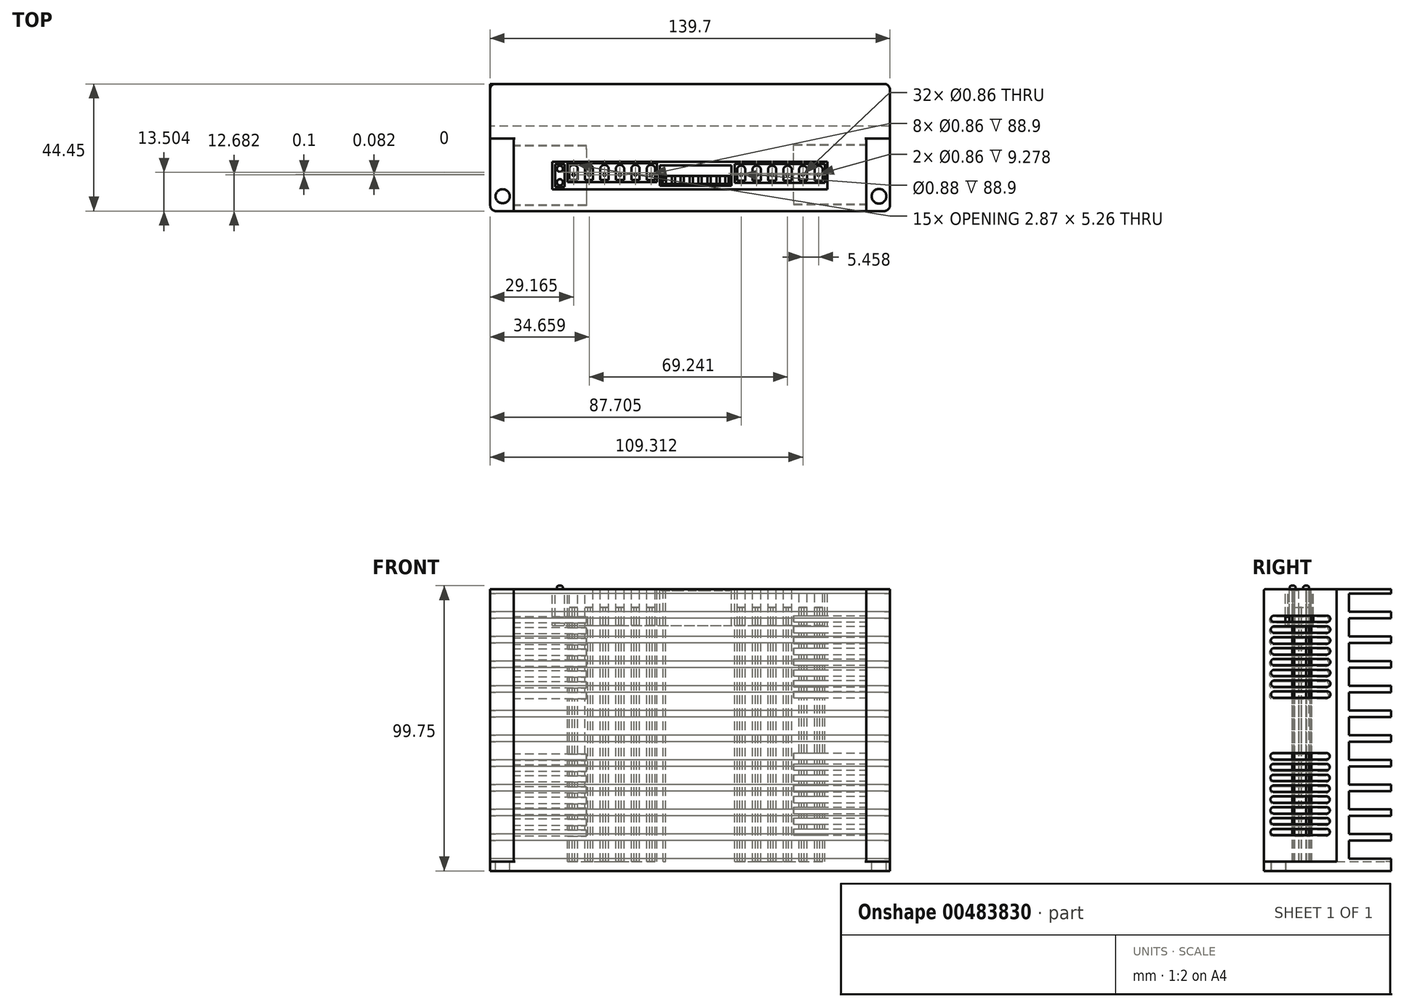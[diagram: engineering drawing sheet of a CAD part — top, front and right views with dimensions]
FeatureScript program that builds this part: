
annotation { "Feature Type Name" : "Feature", "Feature Type Description" : "" }
export const myFeature = defineFeature(function(context is Context, id is Id, definition is map)
    precondition{}
    {
        {
            var Q0;
            Q0=qCreatedBy(makeId("Top.planeOp"),FACE);
            var sketch = newSketch(context, id + "F0", { "sketchPlane" : qUnion([Q0])});
            skLineSegment(sketch, "E0.bottom", {"start": v(61.6, 12.7) * mm, "end": v(-61.6, 12.7) * mm});
            skLineSegment(sketch, "E0.top", {"start": v(61.6, -12.7) * mm, "end": v(-61.6, -12.7) * mm});
            skLineSegment(sketch, "E0.left", {"start": v(61.6, 12.7) * mm, "end": v(61.6, -12.7) * mm});
            skLineSegment(sketch, "E0.right", {"start": v(-61.6, 12.7) * mm, "end": v(-61.6, -12.7) * mm});
            skPoint(sketch, "E0.middle", {"position": v(0, 0) * mm});
            skLineSegment(sketch, "E1.bottom", {"start": v(69.85, 12.7) * mm, "end": v(-69.85, 12.7) * mm});
            skLineSegment(sketch, "E1.top", {"start": v(69.85, 31.75) * mm, "end": v(-69.85, 31.75) * mm});
            skLineSegment(sketch, "E1.left", {"start": v(69.85, 12.7) * mm, "end": v(69.85, 31.75) * mm});
            skLineSegment(sketch, "E1.right", {"start": v(-69.85, 12.7) * mm, "end": v(-69.85, 31.75) * mm});
            skPoint(sketch, "E1.middle", {"position": v(0, 22.23) * mm});
            skLineSegment(sketch, "E2.bottom", {"start": v(-48.06, -5.18) * mm, "end": v(48.06, -5.18) * mm});
            skLineSegment(sketch, "E2.top", {"start": v(-48.06, 4.6) * mm, "end": v(48.06, 4.6) * mm});
            skLineSegment(sketch, "E2.left", {"start": v(-48.06, 4.6) * mm, "end": v(-48.06, -5.18) * mm});
            skLineSegment(sketch, "E2.right", {"start": v(48.06, 4.6) * mm, "end": v(48.06, -5.18) * mm});
            skLineSegment(sketch, "E3.bottom", {"start": v(-47.05, 3.69) * mm, "end": v(-43.77, 3.69) * mm});
            skLineSegment(sketch, "E3.top", {"start": v(-47.05, -4.28) * mm, "end": v(-43.77, -4.28) * mm});
            skLineSegment(sketch, "E3.left", {"start": v(-47.05, 3.69) * mm, "end": v(-47.05, -4.28) * mm});
            skLineSegment(sketch, "E3.right", {"start": v(-43.77, 3.69) * mm, "end": v(-43.77, -4.28) * mm});
            skLineSegment(sketch, "E4.bottom", {"start": v(-42.75, 4.07) * mm, "end": v(-11.5, 4.07) * mm});
            skLineSegment(sketch, "E4.top", {"start": v(-42.75, -2.56) * mm, "end": v(-11.5, -2.56) * mm});
            skLineSegment(sketch, "E4.left", {"start": v(-42.75, 4.07) * mm, "end": v(-42.75, -2.56) * mm});
            skLineSegment(sketch, "E4.right", {"start": v(-11.5, 4.07) * mm, "end": v(-11.5, -2.56) * mm});
            skLineSegment(sketch, "E5.bottom", {"start": v(15.6, 3.79) * mm, "end": v(47.16, 3.79) * mm});
            skLineSegment(sketch, "E5.top", {"start": v(15.6, -2.8) * mm, "end": v(47.16, -2.8) * mm});
            skLineSegment(sketch, "E5.left", {"start": v(15.6, 3.79) * mm, "end": v(15.6, -2.8) * mm});
            skLineSegment(sketch, "E5.right", {"start": v(47.16, 3.79) * mm, "end": v(47.16, -2.8) * mm});
            skLineSegment(sketch, "E6.bottom", {"start": v(-10.49, 3.24) * mm, "end": v(14.52, 3.24) * mm});
            skLineSegment(sketch, "E6.top", {"start": v(-10.49, -3.8) * mm, "end": v(14.52, -3.8) * mm});
            skLineSegment(sketch, "E6.left", {"start": v(-10.49, 3.24) * mm, "end": v(-10.49, -3.8) * mm});
            skLineSegment(sketch, "E6.right", {"start": v(14.52, 3.24) * mm, "end": v(14.52, -3.8) * mm});
            skLineSegment(sketch, "E7", {"start": v(-42.12, -1.82) * mm, "end": v(-39.25, -1.82) * mm});
            skLineSegment(sketch, "E8", {"start": v(-42.12, -1.82) * mm, "end": v(-42.12, 2.37) * mm});
            skLineSegment(sketch, "E9", {"start": v(-39.25, -1.82) * mm, "end": v(-39.25, 2.37) * mm});
            skArc(sketch, "E10", {"start": v(-39.25, 2.37) * mm, "mid": v(-40.68, 3.43) * mm, "end": v(-42.12, 2.37) * mm});
            skCircle(sketch, "E11", {"center": v(-45.45, 2.08) * mm, "radius": 1.05 * mm});
            skCircle(sketch, "E12", {"center": v(-45.45, -2.65) * mm, "radius": 1.07 * mm});
            skLineSegment(sketch, "E13.1.0.0", {"start": v(-36.7, -1.83) * mm, "end": v(-36.7, 2.36) * mm});
            skLineSegment(sketch, "E13.1.0.1", {"start": v(-36.7, -1.83) * mm, "end": v(-33.84, -1.83) * mm});
            skLineSegment(sketch, "E13.1.0.2", {"start": v(-33.84, -1.83) * mm, "end": v(-33.84, 2.36) * mm});
            skArc(sketch, "E13.1.0.3", {"start": v(-33.84, 2.36) * mm, "mid": v(-35.27, 3.43) * mm, "end": v(-36.7, 2.36) * mm});
            skLineSegment(sketch, "E13.2.0.0", {"start": v(-31.3, -1.83) * mm, "end": v(-31.3, 2.36) * mm});
            skLineSegment(sketch, "E13.2.0.1", {"start": v(-31.3, -1.83) * mm, "end": v(-28.43, -1.83) * mm});
            skLineSegment(sketch, "E13.2.0.2", {"start": v(-28.43, -1.83) * mm, "end": v(-28.43, 2.36) * mm});
            skArc(sketch, "E13.2.0.3", {"start": v(-28.43, 2.36) * mm, "mid": v(-29.86, 3.42) * mm, "end": v(-31.3, 2.36) * mm});
            skLineSegment(sketch, "E13.3.0.0", {"start": v(-25.89, -1.84) * mm, "end": v(-25.89, 2.35) * mm});
            skLineSegment(sketch, "E13.3.0.1", {"start": v(-25.89, -1.84) * mm, "end": v(-23.02, -1.84) * mm});
            skLineSegment(sketch, "E13.3.0.2", {"start": v(-23.02, -1.84) * mm, "end": v(-23.02, 2.35) * mm});
            skArc(sketch, "E13.3.0.3", {"start": v(-23.02, 2.35) * mm, "mid": v(-24.45, 3.42) * mm, "end": v(-25.89, 2.35) * mm});
            skLineSegment(sketch, "E13.4.0.0", {"start": v(-20.48, -1.84) * mm, "end": v(-20.48, 2.35) * mm});
            skLineSegment(sketch, "E13.4.0.1", {"start": v(-20.48, -1.84) * mm, "end": v(-17.6, -1.84) * mm});
            skLineSegment(sketch, "E13.4.0.2", {"start": v(-17.6, -1.84) * mm, "end": v(-17.6, 2.35) * mm});
            skArc(sketch, "E13.4.0.3", {"start": v(-17.6, 2.35) * mm, "mid": v(-19.04, 3.41) * mm, "end": v(-20.48, 2.35) * mm});
            skLineSegment(sketch, "E13.5.0.0", {"start": v(-15.07, -1.85) * mm, "end": v(-15.07, 2.34) * mm});
            skLineSegment(sketch, "E13.5.0.1", {"start": v(-15.07, -1.85) * mm, "end": v(-12.2, -1.85) * mm});
            skLineSegment(sketch, "E13.5.0.2", {"start": v(-12.2, -1.85) * mm, "end": v(-12.2, 2.34) * mm});
            skArc(sketch, "E13.5.0.3", {"start": v(-12.2, 2.34) * mm, "mid": v(-13.63, 3.4) * mm, "end": v(-15.07, 2.34) * mm});
            skLineSegment(sketch, "E13.direction1", {"start": v(-42.12, -1.82) * mm, "end": v(-36.7, -1.83) * mm, "construction": true});
            skLineSegment(sketch, "E14", {"start": v(16.46, -2.1) * mm, "end": v(19.33, -2.1) * mm});
            skLineSegment(sketch, "E15", {"start": v(16.46, -2.1) * mm, "end": v(16.46, 2.08) * mm});
            skLineSegment(sketch, "E16", {"start": v(19.33, -2.1) * mm, "end": v(19.33, 2.08) * mm});
            skArc(sketch, "E17", {"start": v(19.33, 2.08) * mm, "mid": v(17.9, 3.15) * mm, "end": v(16.46, 2.08) * mm});
            skLineSegment(sketch, "E18.1.0.0", {"start": v(21.87, -2.11) * mm, "end": v(21.87, 2.08) * mm});
            skLineSegment(sketch, "E18.1.0.1", {"start": v(21.87, -2.11) * mm, "end": v(24.74, -2.11) * mm});
            skLineSegment(sketch, "E18.1.0.2", {"start": v(24.74, -2.11) * mm, "end": v(24.74, 2.08) * mm});
            skArc(sketch, "E18.1.0.3", {"start": v(24.74, 2.08) * mm, "mid": v(23.3, 3.14) * mm, "end": v(21.87, 2.08) * mm});
            skLineSegment(sketch, "E18.2.0.0", {"start": v(27.28, -2.12) * mm, "end": v(27.28, 2.07) * mm});
            skLineSegment(sketch, "E18.2.0.1", {"start": v(27.28, -2.12) * mm, "end": v(30.15, -2.12) * mm});
            skLineSegment(sketch, "E18.2.0.2", {"start": v(30.15, -2.12) * mm, "end": v(30.15, 2.07) * mm});
            skArc(sketch, "E18.2.0.3", {"start": v(30.15, 2.07) * mm, "mid": v(28.71, 3.14) * mm, "end": v(27.28, 2.07) * mm});
            skLineSegment(sketch, "E18.3.0.0", {"start": v(32.69, -2.12) * mm, "end": v(32.69, 2.07) * mm});
            skLineSegment(sketch, "E18.3.0.1", {"start": v(32.69, -2.12) * mm, "end": v(35.56, -2.12) * mm});
            skLineSegment(sketch, "E18.3.0.2", {"start": v(35.56, -2.12) * mm, "end": v(35.56, 2.07) * mm});
            skArc(sketch, "E18.3.0.3", {"start": v(35.56, 2.07) * mm, "mid": v(34.12, 3.13) * mm, "end": v(32.69, 2.07) * mm});
            skLineSegment(sketch, "E18.4.0.0", {"start": v(38.1, -2.13) * mm, "end": v(38.1, 2.06) * mm});
            skLineSegment(sketch, "E18.4.0.1", {"start": v(38.1, -2.13) * mm, "end": v(40.97, -2.13) * mm});
            skLineSegment(sketch, "E18.4.0.2", {"start": v(40.97, -2.13) * mm, "end": v(40.97, 2.06) * mm});
            skArc(sketch, "E18.4.0.3", {"start": v(40.97, 2.06) * mm, "mid": v(39.53, 3.13) * mm, "end": v(38.1, 2.06) * mm});
            skLineSegment(sketch, "E18.5.0.0", {"start": v(43.5, -2.13) * mm, "end": v(43.5, 2.06) * mm});
            skLineSegment(sketch, "E18.5.0.1", {"start": v(43.5, -2.13) * mm, "end": v(46.38, -2.13) * mm});
            skLineSegment(sketch, "E18.5.0.2", {"start": v(46.38, -2.13) * mm, "end": v(46.38, 2.06) * mm});
            skArc(sketch, "E18.5.0.3", {"start": v(46.38, 2.06) * mm, "mid": v(44.94, 3.12) * mm, "end": v(43.5, 2.06) * mm});
            skLineSegment(sketch, "E18.direction1", {"start": v(16.46, -2.1) * mm, "end": v(21.87, -2.11) * mm, "construction": true});
            skLineSegment(sketch, "E19.bottom", {"start": v(-9.96, -0.38) * mm, "end": v(13.92, -0.38) * mm});
            skLineSegment(sketch, "E19.top", {"start": v(-9.96, -3.2) * mm, "end": v(13.92, -3.2) * mm});
            skLineSegment(sketch, "E19.left", {"start": v(-9.96, -0.38) * mm, "end": v(-9.96, -3.2) * mm});
            skLineSegment(sketch, "E19.right", {"start": v(13.92, -0.38) * mm, "end": v(13.92, -3.2) * mm});
            skLineSegment(sketch, "E20.bottom", {"start": v(-9.52, -0.44) * mm, "end": v(-8.38, -0.44) * mm});
            skLineSegment(sketch, "E20.top", {"start": v(-9.52, -3.2) * mm, "end": v(-8.38, -3.2) * mm});
            skLineSegment(sketch, "E20.left", {"start": v(-9.52, -0.44) * mm, "end": v(-9.52, -3.2) * mm});
            skLineSegment(sketch, "E20.right", {"start": v(-8.38, -0.44) * mm, "end": v(-8.38, -3.2) * mm});
            skPoint(sketch, "E21.oppositeSnap0", {"position": v(-9.52, -1.82) * mm});
            skLineSegment(sketch, "E21.bottom", {"start": v(-9.34, -0.44) * mm, "end": v(-8.55, -0.44) * mm});
            skLineSegment(sketch, "E21.top", {"start": v(-9.34, -1.82) * mm, "end": v(-8.55, -1.82) * mm});
            skLineSegment(sketch, "E21.left", {"start": v(-9.34, -0.44) * mm, "end": v(-9.34, -1.82) * mm});
            skLineSegment(sketch, "E21.right", {"start": v(-8.55, -0.44) * mm, "end": v(-8.55, -1.82) * mm});
            skLineSegment(sketch, "E22.1.0.0", {"start": v(-5.25, -0.44) * mm, "end": v(-5.25, -3.2) * mm});
            skLineSegment(sketch, "E22.1.0.1", {"start": v(-6.22, -0.44) * mm, "end": v(-5.42, -0.44) * mm});
            skLineSegment(sketch, "E22.1.0.2", {"start": v(-6.4, -0.44) * mm, "end": v(-5.25, -0.44) * mm});
            skLineSegment(sketch, "E22.1.0.3", {"start": v(-5.42, -0.44) * mm, "end": v(-5.42, -1.82) * mm});
            skLineSegment(sketch, "E22.1.0.4", {"start": v(-6.22, -0.44) * mm, "end": v(-6.22, -1.82) * mm});
            skLineSegment(sketch, "E22.1.0.5", {"start": v(-6.4, -0.44) * mm, "end": v(-6.4, -3.2) * mm});
            skLineSegment(sketch, "E22.1.0.6", {"start": v(-6.4, -3.2) * mm, "end": v(-5.25, -3.2) * mm});
            skLineSegment(sketch, "E22.1.0.7", {"start": v(-6.22, -1.82) * mm, "end": v(-5.42, -1.82) * mm});
            skLineSegment(sketch, "E22.2.0.0", {"start": v(-2.13, -0.44) * mm, "end": v(-2.13, -3.2) * mm});
            skLineSegment(sketch, "E22.2.0.1", {"start": v(-3.1, -0.44) * mm, "end": v(-2.3, -0.44) * mm});
            skLineSegment(sketch, "E22.2.0.2", {"start": v(-3.28, -0.44) * mm, "end": v(-2.13, -0.44) * mm});
            skLineSegment(sketch, "E22.2.0.3", {"start": v(-2.3, -0.44) * mm, "end": v(-2.3, -1.82) * mm});
            skLineSegment(sketch, "E22.2.0.4", {"start": v(-3.1, -0.44) * mm, "end": v(-3.1, -1.82) * mm});
            skLineSegment(sketch, "E22.2.0.5", {"start": v(-3.28, -0.44) * mm, "end": v(-3.28, -3.2) * mm});
            skLineSegment(sketch, "E22.2.0.6", {"start": v(-3.28, -3.2) * mm, "end": v(-2.13, -3.2) * mm});
            skLineSegment(sketch, "E22.2.0.7", {"start": v(-3.1, -1.82) * mm, "end": v(-2.3, -1.82) * mm});
            skLineSegment(sketch, "E22.3.0.0", {"start": v(1, -0.44) * mm, "end": v(1, -3.2) * mm});
            skLineSegment(sketch, "E22.3.0.1", {"start": v(0.03, -0.44) * mm, "end": v(0.82, -0.44) * mm});
            skLineSegment(sketch, "E22.3.0.2", {"start": v(-0.15, -0.44) * mm, "end": v(1, -0.44) * mm});
            skLineSegment(sketch, "E22.3.0.3", {"start": v(0.82, -0.44) * mm, "end": v(0.82, -1.82) * mm});
            skLineSegment(sketch, "E22.3.0.4", {"start": v(0.03, -0.44) * mm, "end": v(0.03, -1.82) * mm});
            skLineSegment(sketch, "E22.3.0.5", {"start": v(-0.15, -0.44) * mm, "end": v(-0.15, -3.2) * mm});
            skLineSegment(sketch, "E22.3.0.6", {"start": v(-0.15, -3.2) * mm, "end": v(1, -3.2) * mm});
            skLineSegment(sketch, "E22.3.0.7", {"start": v(0.03, -1.82) * mm, "end": v(0.82, -1.82) * mm});
            skLineSegment(sketch, "E22.4.0.0", {"start": v(4.12, -0.44) * mm, "end": v(4.12, -3.2) * mm});
            skLineSegment(sketch, "E22.4.0.1", {"start": v(3.15, -0.44) * mm, "end": v(3.95, -0.44) * mm});
            skLineSegment(sketch, "E22.4.0.2", {"start": v(2.97, -0.44) * mm, "end": v(4.12, -0.44) * mm});
            skLineSegment(sketch, "E22.4.0.3", {"start": v(3.95, -0.44) * mm, "end": v(3.95, -1.82) * mm});
            skLineSegment(sketch, "E22.4.0.4", {"start": v(3.15, -0.44) * mm, "end": v(3.15, -1.82) * mm});
            skLineSegment(sketch, "E22.4.0.5", {"start": v(2.97, -0.44) * mm, "end": v(2.97, -3.2) * mm});
            skLineSegment(sketch, "E22.4.0.6", {"start": v(2.97, -3.2) * mm, "end": v(4.12, -3.2) * mm});
            skLineSegment(sketch, "E22.4.0.7", {"start": v(3.15, -1.82) * mm, "end": v(3.95, -1.82) * mm});
            skLineSegment(sketch, "E22.5.0.0", {"start": v(7.25, -0.44) * mm, "end": v(7.25, -3.2) * mm});
            skLineSegment(sketch, "E22.5.0.1", {"start": v(6.28, -0.44) * mm, "end": v(7.07, -0.44) * mm});
            skLineSegment(sketch, "E22.5.0.2", {"start": v(6.1, -0.44) * mm, "end": v(7.25, -0.44) * mm});
            skLineSegment(sketch, "E22.5.0.3", {"start": v(7.07, -0.44) * mm, "end": v(7.07, -1.82) * mm});
            skLineSegment(sketch, "E22.5.0.4", {"start": v(6.28, -0.44) * mm, "end": v(6.28, -1.82) * mm});
            skLineSegment(sketch, "E22.5.0.5", {"start": v(6.1, -0.44) * mm, "end": v(6.1, -3.2) * mm});
            skLineSegment(sketch, "E22.5.0.6", {"start": v(6.1, -3.2) * mm, "end": v(7.25, -3.2) * mm});
            skLineSegment(sketch, "E22.5.0.7", {"start": v(6.28, -1.82) * mm, "end": v(7.07, -1.82) * mm});
            skLineSegment(sketch, "E22.6.0.0", {"start": v(10.37, -0.44) * mm, "end": v(10.37, -3.2) * mm});
            skLineSegment(sketch, "E22.6.0.1", {"start": v(9.4, -0.44) * mm, "end": v(10.2, -0.44) * mm});
            skLineSegment(sketch, "E22.6.0.2", {"start": v(9.22, -0.44) * mm, "end": v(10.37, -0.44) * mm});
            skLineSegment(sketch, "E22.6.0.3", {"start": v(10.2, -0.44) * mm, "end": v(10.2, -1.82) * mm});
            skLineSegment(sketch, "E22.6.0.4", {"start": v(9.4, -0.44) * mm, "end": v(9.4, -1.82) * mm});
            skLineSegment(sketch, "E22.6.0.5", {"start": v(9.22, -0.44) * mm, "end": v(9.22, -3.2) * mm});
            skLineSegment(sketch, "E22.6.0.6", {"start": v(9.22, -3.2) * mm, "end": v(10.37, -3.2) * mm});
            skLineSegment(sketch, "E22.6.0.7", {"start": v(9.4, -1.82) * mm, "end": v(10.2, -1.82) * mm});
            skLineSegment(sketch, "E22.7.0.0", {"start": v(13.5, -0.44) * mm, "end": v(13.5, -3.2) * mm});
            skLineSegment(sketch, "E22.7.0.1", {"start": v(12.53, -0.44) * mm, "end": v(13.32, -0.44) * mm});
            skLineSegment(sketch, "E22.7.0.2", {"start": v(12.35, -0.44) * mm, "end": v(13.5, -0.44) * mm});
            skLineSegment(sketch, "E22.7.0.3", {"start": v(13.32, -0.44) * mm, "end": v(13.32, -1.82) * mm});
            skLineSegment(sketch, "E22.7.0.4", {"start": v(12.53, -0.44) * mm, "end": v(12.53, -1.82) * mm});
            skLineSegment(sketch, "E22.7.0.5", {"start": v(12.35, -0.44) * mm, "end": v(12.35, -3.2) * mm});
            skLineSegment(sketch, "E22.7.0.6", {"start": v(12.35, -3.2) * mm, "end": v(13.5, -3.2) * mm});
            skLineSegment(sketch, "E22.7.0.7", {"start": v(12.53, -1.82) * mm, "end": v(13.32, -1.82) * mm});
            skLineSegment(sketch, "E22.direction1", {"start": v(-8.38, -3.2) * mm, "end": v(-5.25, -3.2) * mm, "construction": true});
            skCircle(sketch, "E23", {"center": v(-40.66, 0) * mm, "radius": 0.44 * mm});
            skCircle(sketch, "E24", {"center": v(-35.2, 0) * mm, "radius": 0.43 * mm});
            skCircle(sketch, "E25", {"center": v(-29.85, 0) * mm, "radius": 0.43 * mm});
            skCircle(sketch, "E26", {"center": v(-24.47, 0) * mm, "radius": 0.43 * mm});
            skCircle(sketch, "E27", {"center": v(-19.05, 0.08) * mm, "radius": 0.43 * mm});
            skCircle(sketch, "E28", {"center": v(-13.6, 0) * mm, "radius": 0.43 * mm});
            skCircle(sketch, "E29", {"center": v(17.86, -0.02) * mm, "radius": 0.44 * mm});
            skCircle(sketch, "E30", {"center": v(23.33, -0.02) * mm, "radius": 0.43 * mm});
            skCircle(sketch, "E31", {"center": v(28.67, -0.02) * mm, "radius": 0.43 * mm});
            skCircle(sketch, "E32", {"center": v(34.05, -0.02) * mm, "radius": 0.43 * mm});
            skCircle(sketch, "E33", {"center": v(39.46, 0.06) * mm, "radius": 0.43 * mm});
            skCircle(sketch, "E34", {"center": v(44.92, -0.02) * mm, "radius": 0.43 * mm});
            skPoint(sketch, "E35", {"position": v(21.87, -0.02) * mm});
            skSolve(sketch);
        }
        {
            var Q0;
            Q0=makeQuery(id+"F0.imprint","IMPRINT",FACE,{"disambiguationData":[TD([[makeQuery(id+"F0.imprint","IMPRINT",EDGE,{"derivedFrom":sQuery(id+"F0.wireOp",EDGE,"E0.top")}),-1.0]])]});
            var Q1;
            Q1=makeQuery(id+"F0.imprint","IMPRINT",FACE,{"disambiguationData":[TD([[makeQuery(id+"F0.imprint","IMPRINT",EDGE,{"derivedFrom":sQuery(id+"F0.wireOp",EDGE,"E2.bottom")}),1.0]])]});
            var Q2;
            Q2=makeQuery(id+"F0.imprint","IMPRINT",FACE,{"disambiguationData":[TD([[makeQuery(id+"F0.imprint","IMPRINT",EDGE,{"derivedFrom":sQuery(id+"F0.wireOp",EDGE,"E3.bottom")}),-1.0]])]});
            var Q3;
            Q3=makeQuery(id+"F0.imprint","IMPRINT",FACE,{"disambiguationData":[TD([[makeQuery(id+"F0.imprint","IMPRINT",EDGE,{"derivedFrom":sQuery(id+"F0.wireOp",EDGE,"E19.bottom")}),-1.0]])]});
            var Q4;
            Q4=makeQuery(id+"F0.imprint","IMPRINT",FACE,{"disambiguationData":[TD([[makeQuery(id+"F0.imprint","IMPRINT",EDGE,{"derivedFrom":sQuery(id+"F0.wireOp",EDGE,"E6.bottom")}),-1.0]])]});
            var Q5;
            Q5=makeQuery(id+"F0.imprint","IMPRINT",FACE,{"disambiguationData":[TD([[makeQuery(id+"F0.imprint","IMPRINT",EDGE,{"derivedFrom":sQuery(id+"F0.wireOp",EDGE,"E18.4.0.0")}),-1.0]])]});
            var Q6;
            Q6=makeQuery(id+"F0.imprint","IMPRINT",FACE,{"disambiguationData":[TD([[makeQuery(id+"F0.imprint","IMPRINT",EDGE,{"derivedFrom":sQuery(id+"F0.wireOp",EDGE,"E18.5.0.0")}),-1.0]])]});
            var Q7;
            Q7=makeQuery(id+"F0.imprint","IMPRINT",FACE,{"disambiguationData":[TD([[makeQuery(id+"F0.imprint","IMPRINT",EDGE,{"derivedFrom":sQuery(id+"F0.wireOp",EDGE,"E7")}),1.0]])]});
            var Q8;
            Q8=makeQuery(id+"F0.imprint","IMPRINT",FACE,{"disambiguationData":[TD([[makeQuery(id+"F0.imprint","IMPRINT",EDGE,{"derivedFrom":sQuery(id+"F0.wireOp",EDGE,"E13.1.0.0")}),-1.0]])]});
            var Q9;
            Q9=makeQuery(id+"F0.imprint","IMPRINT",FACE,{"disambiguationData":[TD([[makeQuery(id+"F0.imprint","IMPRINT",EDGE,{"derivedFrom":sQuery(id+"F0.wireOp",EDGE,"E13.2.0.0")}),-1.0]])]});
            var Q10;
            Q10=makeQuery(id+"F0.imprint","IMPRINT",FACE,{"disambiguationData":[TD([[makeQuery(id+"F0.imprint","IMPRINT",EDGE,{"derivedFrom":sQuery(id+"F0.wireOp",EDGE,"E13.3.0.0")}),-1.0]])]});
            var Q11;
            Q11=makeQuery(id+"F0.imprint","IMPRINT",FACE,{"disambiguationData":[TD([[makeQuery(id+"F0.imprint","IMPRINT",EDGE,{"derivedFrom":sQuery(id+"F0.wireOp",EDGE,"E13.4.0.0")}),-1.0]])]});
            var Q12;
            Q12=makeQuery(id+"F0.imprint","IMPRINT",FACE,{"disambiguationData":[TD([[makeQuery(id+"F0.imprint","IMPRINT",EDGE,{"derivedFrom":sQuery(id+"F0.wireOp",EDGE,"E13.5.0.0")}),-1.0]])]});
            var Q13;
            Q13=makeQuery(id+"F0.imprint","IMPRINT",FACE,{"disambiguationData":[TD([[makeQuery(id+"F0.imprint","IMPRINT",EDGE,{"derivedFrom":sQuery(id+"F0.wireOp",EDGE,"E14")}),1.0]])]});
            var Q14;
            Q14=makeQuery(id+"F0.imprint","IMPRINT",FACE,{"disambiguationData":[TD([[makeQuery(id+"F0.imprint","IMPRINT",EDGE,{"derivedFrom":sQuery(id+"F0.wireOp",EDGE,"E18.1.0.0")}),-1.0]])]});
            var Q15;
            Q15=makeQuery(id+"F0.imprint","IMPRINT",FACE,{"disambiguationData":[TD([[makeQuery(id+"F0.imprint","IMPRINT",EDGE,{"derivedFrom":sQuery(id+"F0.wireOp",EDGE,"E18.2.0.0")}),-1.0]])]});
            var Q16;
            Q16=makeQuery(id+"F0.imprint","IMPRINT",FACE,{"disambiguationData":[TD([[makeQuery(id+"F0.imprint","IMPRINT",EDGE,{"derivedFrom":sQuery(id+"F0.wireOp",EDGE,"E18.3.0.0")}),-1.0]])]});
            var Q17;
            Q17=makeQuery(id+"F0.imprint","IMPRINT",FACE,{"disambiguationData":[TD([[makeQuery(id+"F0.imprint","IMPRINT",EDGE,{"derivedFrom":sQuery(id+"F0.wireOp",EDGE,"E11")}),1.0]])]});
            var Q18;
            Q18=makeQuery(id+"F0.imprint","IMPRINT",FACE,{"disambiguationData":[TD([[makeQuery(id+"F0.imprint","IMPRINT",EDGE,{"derivedFrom":sQuery(id+"F0.wireOp",EDGE,"E12")}),1.0]])]});
            var Q19;
            {var subQ2=sQuery(id+"F0.wireOp",EDGE,"E22.2.0.0");Q19=makeQuery(id+"F0.imprint","IMPRINT",FACE,{"disambiguationData":[TD([[makeQuery(id+"F0.imprint","IMPRINT",EDGE,{"derivedFrom":subQ2}),-1.0]])]});}
            var Q20;
            {var subQ2=sQuery(id+"F0.wireOp",EDGE,"E22.5.0.0");Q20=makeQuery(id+"F0.imprint","IMPRINT",FACE,{"disambiguationData":[TD([[makeQuery(id+"F0.imprint","IMPRINT",EDGE,{"derivedFrom":subQ2}),-1.0]])]});}
            var Q21;
            {var subQ0=sQuery(id+"F0.wireOp",EDGE,"E22.1.0.3");Q21=makeQuery(id+"F0.imprint","IMPRINT",FACE,{"disambiguationData":[TD([[makeQuery(id+"F0.imprint","IMPRINT",EDGE,{"derivedFrom":subQ0}),-1.0]])]});}
            var Q22;
            {var subQ2=sQuery(id+"F0.wireOp",EDGE,"E22.6.0.0");Q22=makeQuery(id+"F0.imprint","IMPRINT",FACE,{"disambiguationData":[TD([[makeQuery(id+"F0.imprint","IMPRINT",EDGE,{"derivedFrom":subQ2}),-1.0]])]});}
            var Q23;
            {var subQ0=sQuery(id+"F0.wireOp",EDGE,"E22.2.0.3");Q23=makeQuery(id+"F0.imprint","IMPRINT",FACE,{"disambiguationData":[TD([[makeQuery(id+"F0.imprint","IMPRINT",EDGE,{"derivedFrom":subQ0}),-1.0]])]});}
            var Q24;
            {var subQ2=sQuery(id+"F0.wireOp",EDGE,"E22.3.0.0");Q24=makeQuery(id+"F0.imprint","IMPRINT",FACE,{"disambiguationData":[TD([[makeQuery(id+"F0.imprint","IMPRINT",EDGE,{"derivedFrom":subQ2}),-1.0]])]});}
            var Q25;
            {var subQ2=sQuery(id+"F0.wireOp",EDGE,"E22.7.0.0");Q25=makeQuery(id+"F0.imprint","IMPRINT",FACE,{"disambiguationData":[TD([[makeQuery(id+"F0.imprint","IMPRINT",EDGE,{"derivedFrom":subQ2}),-1.0]])]});}
            var Q26;
            {var subQ2=sQuery(id+"F0.wireOp",EDGE,"E22.4.0.0");Q26=makeQuery(id+"F0.imprint","IMPRINT",FACE,{"disambiguationData":[TD([[makeQuery(id+"F0.imprint","IMPRINT",EDGE,{"derivedFrom":subQ2}),-1.0]])]});}
            var Q27;
            Q27=makeQuery(id+"F0.imprint","IMPRINT",FACE,{"disambiguationData":[TD([[makeQuery(id+"F0.imprint","IMPRINT",EDGE,{"derivedFrom":sQuery(id+"F0.wireOp",EDGE,"E20.top")}),1.0]])]});
            var Q28;
            {var subQ0=sQuery(id+"F0.wireOp",EDGE,"E22.5.0.3");Q28=makeQuery(id+"F0.imprint","IMPRINT",FACE,{"disambiguationData":[TD([[makeQuery(id+"F0.imprint","IMPRINT",EDGE,{"derivedFrom":subQ0}),-1.0]])]});}
            var Q29;
            {var subQ0=sQuery(id+"F0.wireOp",EDGE,"E22.7.0.3");Q29=makeQuery(id+"F0.imprint","IMPRINT",FACE,{"disambiguationData":[TD([[makeQuery(id+"F0.imprint","IMPRINT",EDGE,{"derivedFrom":subQ0}),-1.0]])]});}
            var Q30;
            {var subQ0=sQuery(id+"F0.wireOp",EDGE,"E22.6.0.3");Q30=makeQuery(id+"F0.imprint","IMPRINT",FACE,{"disambiguationData":[TD([[makeQuery(id+"F0.imprint","IMPRINT",EDGE,{"derivedFrom":subQ0}),-1.0]])]});}
            var Q31;
            {var subQ0=sQuery(id+"F0.wireOp",EDGE,"E22.4.0.3");Q31=makeQuery(id+"F0.imprint","IMPRINT",FACE,{"disambiguationData":[TD([[makeQuery(id+"F0.imprint","IMPRINT",EDGE,{"derivedFrom":subQ0}),-1.0]])]});}
            var Q32;
            {var subQ2=sQuery(id+"F0.wireOp",EDGE,"E22.1.0.0");Q32=makeQuery(id+"F0.imprint","IMPRINT",FACE,{"disambiguationData":[TD([[makeQuery(id+"F0.imprint","IMPRINT",EDGE,{"derivedFrom":subQ2}),-1.0]])]});}
            var Q33;
            {var subQ0=sQuery(id+"F0.wireOp",EDGE,"E22.3.0.3");Q33=makeQuery(id+"F0.imprint","IMPRINT",FACE,{"disambiguationData":[TD([[makeQuery(id+"F0.imprint","IMPRINT",EDGE,{"derivedFrom":subQ0}),-1.0]])]});}
            var Q34;
            Q34=makeQuery(id+"F0.imprint","IMPRINT",FACE,{"disambiguationData":[TD([[makeQuery(id+"F0.imprint","IMPRINT",EDGE,{"derivedFrom":sQuery(id+"F0.wireOp",EDGE,"E21.bottom")}),-1.0]])]});
            extrude(context, id + "F1", {"entities" : qUnion([Q0, Q1, Q2, Q3, Q4, Q5, Q6, Q7, Q8, Q9, Q10, Q11, Q12, Q13, Q14, Q15, Q16, Q17, Q18, Q19, Q20, Q21, Q22, Q23, Q24, Q25, Q26, Q27, Q28, Q29, Q30, Q31, Q32, Q33, Q34]), "oppositeDirection" : true, "depth" : 95.25 * mm});
        }
        {
            var Q0;
            Q0=makeQuery(id+"F0.imprint","IMPRINT",FACE,{"disambiguationData":[TD([[makeQuery(id+"F0.imprint","IMPRINT",EDGE,{"derivedFrom":sQuery(id+"F0.wireOp",EDGE,"E1.top")}),1.0]])]});
            extrude(context, id + "F2", {"entities" : qUnion([Q0]), "operationType" : NewBodyOperationType.ADD, "oppositeDirection" : true, "depth" : 95.25 * mm});
        }
        {
            var Q0;
            Q0=makeQuery(id+"F2.opExtrude","SWEPT_FACE",FACE,{"disambiguationData":[OSD([sQuery(id+"F0.wireOp",EDGE,"E1.top")])]});
            var sketch = newSketch(context, id + "F3", { "sketchPlane" : qUnion([Q0])});
            skLineSegment(sketch, "E36.bottom", {"start": v(-69.85, -95.25) * mm, "end": v(69.78, -95.25) * mm});
            skLineSegment(sketch, "E36.top", {"start": v(-69.85, -98.48) * mm, "end": v(69.78, -98.48) * mm});
            skLineSegment(sketch, "E36.left", {"start": v(-69.85, -95.25) * mm, "end": v(-69.85, -98.48) * mm});
            skLineSegment(sketch, "E36.right", {"start": v(69.78, -95.25) * mm, "end": v(69.78, -98.48) * mm});
            skSolve(sketch);
        }
        {
            var Q0;
            Q0=makeQuery(id+"F3.imprint","IMPRINT",FACE,{"disambiguationData":[TD([[makeQuery(id+"F3.imprint","IMPRINT",EDGE,{"derivedFrom":sQuery(id+"F3.wireOp",EDGE,"E36.bottom")}),-1.0]])]});
            extrude(context, id + "F4", {"entities" : qUnion([Q0]), "operationType" : NewBodyOperationType.ADD, "oppositeDirection" : true, "depth" : 44.45 * mm});
        }
        {
            var Q0;
            Q0=makeQuery(id+"F4.boolean.opBoolean","MERGE",FACE,{"derivedFrom":[makeQuery(id+"F2.opExtrude","SWEPT_FACE",FACE,{"disambiguationData":[OSD([sQuery(id+"F0.wireOp",EDGE,"E1.top")])]}),makeQuery(id+"F4.opExtrude","CAP_FACE",FACE,{"disambiguationData":[OSD([sQuery(id+"F3.wireOp",EDGE,"E36.bottom"),sQuery(id+"F3.wireOp",EDGE,"E36.top"),sQuery(id+"F3.wireOp",EDGE,"E36.left"),sQuery(id+"F3.wireOp",EDGE,"E36.right")])],"isStart":true})]});
            var sketch = newSketch(context, id + "F5", { "sketchPlane" : qUnion([Q0])});
            skLineSegment(sketch, "E37.bottom", {"start": v(-69.85, -1.48) * mm, "end": v(69.85, -1.48) * mm});
            skLineSegment(sketch, "E37.top", {"start": v(-69.85, -7.87) * mm, "end": v(69.85, -7.87) * mm});
            skLineSegment(sketch, "E37.left", {"start": v(-69.85, -1.48) * mm, "end": v(-69.85, -7.87) * mm});
            skLineSegment(sketch, "E37.right", {"start": v(69.85, -1.48) * mm, "end": v(69.85, -7.87) * mm});
            skLineSegment(sketch, "E38.1.0.0", {"start": v(-69.85, -16.5) * mm, "end": v(69.85, -16.5) * mm});
            skLineSegment(sketch, "E38.1.0.1", {"start": v(-69.85, -10.12) * mm, "end": v(69.85, -10.12) * mm});
            skLineSegment(sketch, "E38.1.0.2", {"start": v(-69.85, -10.12) * mm, "end": v(-69.85, -16.5) * mm});
            skLineSegment(sketch, "E38.1.0.3", {"start": v(69.85, -10.12) * mm, "end": v(69.85, -16.5) * mm});
            skLineSegment(sketch, "E38.2.0.0", {"start": v(-69.85, -25.14) * mm, "end": v(69.85, -25.14) * mm});
            skLineSegment(sketch, "E38.2.0.1", {"start": v(-69.85, -18.75) * mm, "end": v(69.85, -18.75) * mm});
            skLineSegment(sketch, "E38.2.0.2", {"start": v(-69.85, -18.75) * mm, "end": v(-69.85, -25.14) * mm});
            skLineSegment(sketch, "E38.2.0.3", {"start": v(69.85, -18.75) * mm, "end": v(69.85, -25.14) * mm});
            skLineSegment(sketch, "E38.3.0.0", {"start": v(-69.85, -33.78) * mm, "end": v(69.85, -33.78) * mm});
            skLineSegment(sketch, "E38.3.0.1", {"start": v(-69.85, -27.39) * mm, "end": v(69.85, -27.39) * mm});
            skLineSegment(sketch, "E38.3.0.2", {"start": v(-69.85, -27.39) * mm, "end": v(-69.85, -33.78) * mm});
            skLineSegment(sketch, "E38.3.0.3", {"start": v(69.85, -27.39) * mm, "end": v(69.85, -33.78) * mm});
            skLineSegment(sketch, "E38.4.0.0", {"start": v(-69.85, -42.42) * mm, "end": v(69.85, -42.42) * mm});
            skLineSegment(sketch, "E38.4.0.1", {"start": v(-69.85, -36.02) * mm, "end": v(69.85, -36.02) * mm});
            skLineSegment(sketch, "E38.4.0.2", {"start": v(-69.85, -36.02) * mm, "end": v(-69.85, -42.42) * mm});
            skLineSegment(sketch, "E38.4.0.3", {"start": v(69.85, -36.02) * mm, "end": v(69.85, -42.42) * mm});
            skLineSegment(sketch, "E38.5.0.0", {"start": v(-69.85, -51.05) * mm, "end": v(69.85, -51.05) * mm});
            skLineSegment(sketch, "E38.5.0.1", {"start": v(-69.85, -44.66) * mm, "end": v(69.85, -44.66) * mm});
            skLineSegment(sketch, "E38.5.0.2", {"start": v(-69.85, -44.66) * mm, "end": v(-69.85, -51.05) * mm});
            skLineSegment(sketch, "E38.5.0.3", {"start": v(69.85, -44.66) * mm, "end": v(69.85, -51.05) * mm});
            skLineSegment(sketch, "E38.6.0.0", {"start": v(-69.85, -59.69) * mm, "end": v(69.85, -59.69) * mm});
            skLineSegment(sketch, "E38.6.0.1", {"start": v(-69.85, -53.3) * mm, "end": v(69.85, -53.3) * mm});
            skLineSegment(sketch, "E38.6.0.2", {"start": v(-69.85, -53.3) * mm, "end": v(-69.85, -59.69) * mm});
            skLineSegment(sketch, "E38.6.0.3", {"start": v(69.85, -53.3) * mm, "end": v(69.85, -59.69) * mm});
            skLineSegment(sketch, "E38.7.0.0", {"start": v(-69.85, -68.32) * mm, "end": v(69.85, -68.32) * mm});
            skLineSegment(sketch, "E38.7.0.1", {"start": v(-69.85, -61.93) * mm, "end": v(69.85, -61.93) * mm});
            skLineSegment(sketch, "E38.7.0.2", {"start": v(-69.85, -61.93) * mm, "end": v(-69.85, -68.32) * mm});
            skLineSegment(sketch, "E38.7.0.3", {"start": v(69.85, -61.93) * mm, "end": v(69.85, -68.32) * mm});
            skLineSegment(sketch, "E38.8.0.0", {"start": v(-69.85, -76.96) * mm, "end": v(69.85, -76.96) * mm});
            skLineSegment(sketch, "E38.8.0.1", {"start": v(-69.85, -70.57) * mm, "end": v(69.85, -70.57) * mm});
            skLineSegment(sketch, "E38.8.0.2", {"start": v(-69.85, -70.57) * mm, "end": v(-69.85, -76.96) * mm});
            skLineSegment(sketch, "E38.8.0.3", {"start": v(69.85, -70.57) * mm, "end": v(69.85, -76.96) * mm});
            skLineSegment(sketch, "E38.9.0.0", {"start": v(-69.85, -85.6) * mm, "end": v(69.85, -85.6) * mm});
            skLineSegment(sketch, "E38.9.0.1", {"start": v(-69.85, -79.2) * mm, "end": v(69.85, -79.2) * mm});
            skLineSegment(sketch, "E38.9.0.2", {"start": v(-69.85, -79.2) * mm, "end": v(-69.85, -85.6) * mm});
            skLineSegment(sketch, "E38.9.0.3", {"start": v(69.85, -79.2) * mm, "end": v(69.85, -85.6) * mm});
            skLineSegment(sketch, "E38.10.0.0", {"start": v(-69.85, -94.23) * mm, "end": v(69.85, -94.23) * mm});
            skLineSegment(sketch, "E38.10.0.1", {"start": v(-69.85, -87.84) * mm, "end": v(69.85, -87.84) * mm});
            skLineSegment(sketch, "E38.10.0.2", {"start": v(-69.85, -87.84) * mm, "end": v(-69.85, -94.23) * mm});
            skLineSegment(sketch, "E38.10.0.3", {"start": v(69.85, -87.84) * mm, "end": v(69.85, -94.23) * mm});
            skLineSegment(sketch, "E38.direction1", {"start": v(-69.85, -7.87) * mm, "end": v(-69.85, -16.5) * mm, "construction": true});
            skSolve(sketch);
        }
        {
            var Q0;
            Q0=makeQuery(id+"F5.imprint","IMPRINT",FACE,{"disambiguationData":[TD([[makeQuery(id+"F5.imprint","IMPRINT",EDGE,{"derivedFrom":sQuery(id+"F5.wireOp",EDGE,"E38.10.0.0")}),1.0]])]});
            var Q1;
            Q1=makeQuery(id+"F5.imprint","IMPRINT",FACE,{"disambiguationData":[TD([[makeQuery(id+"F5.imprint","IMPRINT",EDGE,{"derivedFrom":sQuery(id+"F5.wireOp",EDGE,"E38.9.0.0")}),1.0]])]});
            var Q2;
            Q2=makeQuery(id+"F5.imprint","IMPRINT",FACE,{"disambiguationData":[TD([[makeQuery(id+"F5.imprint","IMPRINT",EDGE,{"derivedFrom":sQuery(id+"F5.wireOp",EDGE,"E38.8.0.0")}),1.0]])]});
            var Q3;
            Q3=makeQuery(id+"F5.imprint","IMPRINT",FACE,{"disambiguationData":[TD([[makeQuery(id+"F5.imprint","IMPRINT",EDGE,{"derivedFrom":sQuery(id+"F5.wireOp",EDGE,"E38.7.0.0")}),1.0]])]});
            var Q4;
            Q4=makeQuery(id+"F5.imprint","IMPRINT",FACE,{"disambiguationData":[TD([[makeQuery(id+"F5.imprint","IMPRINT",EDGE,{"derivedFrom":sQuery(id+"F5.wireOp",EDGE,"E38.6.0.0")}),1.0]])]});
            var Q5;
            Q5=makeQuery(id+"F5.imprint","IMPRINT",FACE,{"disambiguationData":[TD([[makeQuery(id+"F5.imprint","IMPRINT",EDGE,{"derivedFrom":sQuery(id+"F5.wireOp",EDGE,"E38.5.0.0")}),1.0]])]});
            var Q6;
            Q6=makeQuery(id+"F5.imprint","IMPRINT",FACE,{"disambiguationData":[TD([[makeQuery(id+"F5.imprint","IMPRINT",EDGE,{"derivedFrom":sQuery(id+"F5.wireOp",EDGE,"E38.4.0.0")}),1.0]])]});
            var Q7;
            Q7=makeQuery(id+"F5.imprint","IMPRINT",FACE,{"disambiguationData":[TD([[makeQuery(id+"F5.imprint","IMPRINT",EDGE,{"derivedFrom":sQuery(id+"F5.wireOp",EDGE,"E38.3.0.0")}),1.0]])]});
            var Q8;
            Q8=makeQuery(id+"F5.imprint","IMPRINT",FACE,{"disambiguationData":[TD([[makeQuery(id+"F5.imprint","IMPRINT",EDGE,{"derivedFrom":sQuery(id+"F5.wireOp",EDGE,"E38.2.0.0")}),1.0]])]});
            var Q9;
            Q9=makeQuery(id+"F5.imprint","IMPRINT",FACE,{"disambiguationData":[TD([[makeQuery(id+"F5.imprint","IMPRINT",EDGE,{"derivedFrom":sQuery(id+"F5.wireOp",EDGE,"E38.1.0.0")}),1.0]])]});
            var Q10;
            Q10=makeQuery(id+"F5.imprint","IMPRINT",FACE,{"disambiguationData":[TD([[makeQuery(id+"F5.imprint","IMPRINT",EDGE,{"derivedFrom":sQuery(id+"F5.wireOp",EDGE,"E37.bottom")}),-1.0]])]});
            extrude(context, id + "F6", {"entities" : qUnion([Q0, Q1, Q2, Q3, Q4, Q5, Q6, Q7, Q8, Q9, Q10]), "operationType" : NewBodyOperationType.REMOVE, "oppositeDirection" : true, "depth" : 14.73 * mm});
        }
        {
            var Q0;
            {var subQ1=sQuery(id+"F0.wireOp",EDGE,"E0.right");var subQ4=sQuery(id+"F3.wireOp",EDGE,"E36.bottom");Q0=makeQuery(id+"F4.boolean.opBoolean","SPLIT",FACE,{"disambiguationData":[TD([makeQuery(id+"F1.opExtrude","SWEPT_FACE",FACE,{"disambiguationData":[OSD([subQ1])]})])],"derivedFrom":makeQuery(id+"F4.opExtrude","SWEPT_FACE",FACE,{"disambiguationData":[OSD([subQ4])]})});}
            var sketch = newSketch(context, id + "F7", { "sketchPlane" : qUnion([Q0])});
            skCircle(sketch, "E39", {"center": v(-65.45, -7.52) * mm, "radius": 2.47 * mm});
            skLineSegment(sketch, "E40", {"start": v(-65.45, -7.52) * mm, "end": v(66.04, -7.52) * mm, "construction": true});
            skCircle(sketch, "E41", {"center": v(66.04, -7.52) * mm, "radius": 2.57 * mm});
            skSolve(sketch);
        }
        {
            var Q0;
            Q0 = qSketchRegion(id + "F7", true);
            extrude(context, id + "F8", {"entities" : qUnion([Q0]), "operationType" : NewBodyOperationType.REMOVE, "endBound" : BoundingType.THROUGH_ALL, "oppositeDirection" : true, "depth" : 25.4 * mm});
        }
        {
            var Q0;
            Q0=makeQuery(id+"F0.imprint","IMPRINT",FACE,{"disambiguationData":[TD([[makeQuery(id+"F0.imprint","IMPRINT",EDGE,{"derivedFrom":sQuery(id+"F0.wireOp",EDGE,"E2.bottom")}),1.0]])]});
            extrude(context, id + "F9", {"entities" : qUnion([Q0]), "operationType" : NewBodyOperationType.REMOVE, "oppositeDirection" : true, "depth" : 12.7 * mm});
        }
        {
            var Q0;
            Q0=makeQuery(id+"F0.imprint","IMPRINT",FACE,{"disambiguationData":[TD([[makeQuery(id+"F0.imprint","IMPRINT",EDGE,{"derivedFrom":sQuery(id+"F0.wireOp",EDGE,"E11")}),1.0]])]});
            var Q1;
            Q1=makeQuery(id+"F0.imprint","IMPRINT",FACE,{"disambiguationData":[TD([[makeQuery(id+"F0.imprint","IMPRINT",EDGE,{"derivedFrom":sQuery(id+"F0.wireOp",EDGE,"E12")}),1.0]])]});
            var Q2;
            Q2=sQuery(id+"F0.wireOp",EDGE,"E12");
            var Q3;
            Q3=sQuery(id+"F0.wireOp",EDGE,"E11");
            extrude(context, id + "F10", {"entities" : qUnion([Q0, Q1]), "surfaceEntities" : qUnion([Q2, Q3]), "depth" : 1.27 * mm});
        }
        {
            var Q0;
            Q0=makeQuery(id+"F10.opExtrude","CAP_EDGE",EDGE,{"disambiguationData":[OSD([sQuery(id+"F0.wireOp",EDGE,"E11")])],"isStart":false});
            var Q1;
            Q1=makeQuery(id+"F10.opExtrude","CAP_EDGE",EDGE,{"disambiguationData":[OSD([sQuery(id+"F0.wireOp",EDGE,"E12")])],"isStart":false});
            fillet(context, id + "F11", {"entities" : qUnion([Q0, Q1]), "radius" : 0.74 * mm, "tangentPropagation" : true, "allowEdgeOverflow" : false});
        }
        {
            var Q0;
            Q0=makeQuery(id+"F0.imprint","IMPRINT",FACE,{"disambiguationData":[TD([[makeQuery(id+"F0.imprint","IMPRINT",EDGE,{"derivedFrom":sQuery(id+"F0.wireOp",EDGE,"E7")}),1.0]])]});
            var Q1;
            Q1=makeQuery(id+"F0.imprint","IMPRINT",FACE,{"disambiguationData":[TD([[makeQuery(id+"F0.imprint","IMPRINT",EDGE,{"derivedFrom":sQuery(id+"F0.wireOp",EDGE,"E13.1.0.0")}),-1.0]])]});
            var Q2;
            Q2=makeQuery(id+"F0.imprint","IMPRINT",FACE,{"disambiguationData":[TD([[makeQuery(id+"F0.imprint","IMPRINT",EDGE,{"derivedFrom":sQuery(id+"F0.wireOp",EDGE,"E13.2.0.0")}),-1.0]])]});
            var Q3;
            Q3=makeQuery(id+"F0.imprint","IMPRINT",FACE,{"disambiguationData":[TD([[makeQuery(id+"F0.imprint","IMPRINT",EDGE,{"derivedFrom":sQuery(id+"F0.wireOp",EDGE,"E13.3.0.0")}),-1.0]])]});
            var Q4;
            Q4=makeQuery(id+"F0.imprint","IMPRINT",FACE,{"disambiguationData":[TD([[makeQuery(id+"F0.imprint","IMPRINT",EDGE,{"derivedFrom":sQuery(id+"F0.wireOp",EDGE,"E13.4.0.0")}),-1.0]])]});
            var Q5;
            Q5=makeQuery(id+"F0.imprint","IMPRINT",FACE,{"disambiguationData":[TD([[makeQuery(id+"F0.imprint","IMPRINT",EDGE,{"derivedFrom":sQuery(id+"F0.wireOp",EDGE,"E13.5.0.0")}),-1.0]])]});
            var Q6;
            Q6=makeQuery(id+"F0.imprint","IMPRINT",FACE,{"disambiguationData":[TD([[makeQuery(id+"F0.imprint","IMPRINT",EDGE,{"derivedFrom":sQuery(id+"F0.wireOp",EDGE,"E14")}),1.0]])]});
            var Q7;
            Q7=makeQuery(id+"F0.imprint","IMPRINT",FACE,{"disambiguationData":[TD([[makeQuery(id+"F0.imprint","IMPRINT",EDGE,{"derivedFrom":sQuery(id+"F0.wireOp",EDGE,"E18.1.0.0")}),-1.0]])]});
            var Q8;
            Q8=makeQuery(id+"F0.imprint","IMPRINT",FACE,{"disambiguationData":[TD([[makeQuery(id+"F0.imprint","IMPRINT",EDGE,{"derivedFrom":sQuery(id+"F0.wireOp",EDGE,"E18.2.0.0")}),-1.0]])]});
            var Q9;
            Q9=makeQuery(id+"F0.imprint","IMPRINT",FACE,{"disambiguationData":[TD([[makeQuery(id+"F0.imprint","IMPRINT",EDGE,{"derivedFrom":sQuery(id+"F0.wireOp",EDGE,"E18.3.0.0")}),-1.0]])]});
            var Q10;
            Q10=makeQuery(id+"F0.imprint","IMPRINT",FACE,{"disambiguationData":[TD([[makeQuery(id+"F0.imprint","IMPRINT",EDGE,{"derivedFrom":sQuery(id+"F0.wireOp",EDGE,"E18.4.0.0")}),-1.0]])]});
            var Q11;
            Q11=makeQuery(id+"F0.imprint","IMPRINT",FACE,{"disambiguationData":[TD([[makeQuery(id+"F0.imprint","IMPRINT",EDGE,{"derivedFrom":sQuery(id+"F0.wireOp",EDGE,"E18.5.0.0")}),-1.0]])]});
            extrude(context, id + "F12", {"entities" : qUnion([Q0, Q1, Q2, Q3, Q4, Q5, Q6, Q7, Q8, Q9, Q10, Q11]), "operationType" : NewBodyOperationType.REMOVE, "oppositeDirection" : true, "depth" : 6.35 * mm});
        }
        {
            var Q0;
            Q0=makeQuery(id+"F0.imprint","IMPRINT",FACE,{"disambiguationData":[TD([[makeQuery(id+"F0.imprint","IMPRINT",EDGE,{"derivedFrom":sQuery(id+"F0.wireOp",EDGE,"E19.bottom")}),-1.0]])]});
            extrude(context, id + "F13", {"entities" : qUnion([Q0]), "operationType" : NewBodyOperationType.REMOVE, "oppositeDirection" : true, "depth" : 0.5 * mm});
        }
        {
            var Q0;
            Q0=makeQuery(id+"F0.imprint","IMPRINT",FACE,{"disambiguationData":[TD([[makeQuery(id+"F0.imprint","IMPRINT",EDGE,{"derivedFrom":sQuery(id+"F0.wireOp",EDGE,"E4.bottom")}),-1.0]])]});
            var Q1;
            Q1=makeQuery(id+"F0.imprint","IMPRINT",FACE,{"disambiguationData":[TD([[makeQuery(id+"F0.imprint","IMPRINT",EDGE,{"derivedFrom":sQuery(id+"F0.wireOp",EDGE,"E5.bottom")}),-1.0]])]});
            extrude(context, id + "F14", {"entities" : qUnion([Q0, Q1]), "oppositeDirection" : true, "depth" : 12.7 * mm});
        }
        {
            var Q0;
            Q0=makeQuery(id+"F1.opExtrude","SWEPT_FACE",FACE,{"disambiguationData":[OSD([sQuery(id+"F0.wireOp",EDGE,"E0.left")])]});
            var sketch = newSketch(context, id + "F15", { "sketchPlane" : qUnion([Q0])});
            skLineSegment(sketch, "E42.bottom", {"start": v(-9.11, -9.19) * mm, "end": v(9.41, -9.19) * mm});
            skLineSegment(sketch, "E42.top", {"start": v(-9.11, -11.42) * mm, "end": v(9.41, -11.42) * mm});
            skArc(sketch, "E43", {"start": v(-9.11, -9.19) * mm, "mid": v(-10.23, -10.3) * mm, "end": v(-9.11, -11.42) * mm});
            skArc(sketch, "E44", {"start": v(9.41, -11.42) * mm, "mid": v(10.53, -10.3) * mm, "end": v(9.41, -9.19) * mm});
            skLineSegment(sketch, "E45.1.0.0", {"start": v(-9.1, -12.97) * mm, "end": v(9.42, -12.97) * mm});
            skLineSegment(sketch, "E45.1.0.1", {"start": v(-9.1, -15.2) * mm, "end": v(9.42, -15.2) * mm});
            skArc(sketch, "E45.1.0.2", {"start": v(-9.1, -12.97) * mm, "mid": v(-10.22, -14.1) * mm, "end": v(-9.1, -15.2) * mm});
            skArc(sketch, "E45.1.0.3", {"start": v(9.42, -15.2) * mm, "mid": v(10.54, -14.1) * mm, "end": v(9.42, -12.97) * mm});
            skLineSegment(sketch, "E45.2.0.0", {"start": v(-9.1, -16.76) * mm, "end": v(9.43, -16.76) * mm});
            skLineSegment(sketch, "E45.2.0.1", {"start": v(-9.1, -19) * mm, "end": v(9.43, -19) * mm});
            skArc(sketch, "E45.2.0.2", {"start": v(-9.1, -16.76) * mm, "mid": v(-10.22, -17.88) * mm, "end": v(-9.1, -19) * mm});
            skArc(sketch, "E45.2.0.3", {"start": v(9.43, -19) * mm, "mid": v(10.54, -17.88) * mm, "end": v(9.43, -16.76) * mm});
            skLineSegment(sketch, "E45.3.0.0", {"start": v(-9.1, -20.54) * mm, "end": v(9.43, -20.54) * mm});
            skLineSegment(sketch, "E45.3.0.1", {"start": v(-9.1, -22.78) * mm, "end": v(9.43, -22.78) * mm});
            skArc(sketch, "E45.3.0.2", {"start": v(-9.1, -20.54) * mm, "mid": v(-10.21, -21.66) * mm, "end": v(-9.1, -22.78) * mm});
            skArc(sketch, "E45.3.0.3", {"start": v(9.43, -22.78) * mm, "mid": v(10.55, -21.66) * mm, "end": v(9.43, -20.54) * mm});
            skLineSegment(sketch, "E45.4.0.0", {"start": v(-9.09, -24.33) * mm, "end": v(9.44, -24.33) * mm});
            skLineSegment(sketch, "E45.4.0.1", {"start": v(-9.09, -26.56) * mm, "end": v(9.44, -26.56) * mm});
            skArc(sketch, "E45.4.0.2", {"start": v(-9.09, -24.33) * mm, "mid": v(-10.2, -25.44) * mm, "end": v(-9.09, -26.56) * mm});
            skArc(sketch, "E45.4.0.3", {"start": v(9.44, -26.56) * mm, "mid": v(10.56, -25.44) * mm, "end": v(9.44, -24.33) * mm});
            skLineSegment(sketch, "E45.5.0.0", {"start": v(-9.08, -28.11) * mm, "end": v(9.45, -28.11) * mm});
            skLineSegment(sketch, "E45.5.0.1", {"start": v(-9.08, -30.35) * mm, "end": v(9.45, -30.35) * mm});
            skArc(sketch, "E45.5.0.2", {"start": v(-9.08, -28.11) * mm, "mid": v(-10.2, -29.23) * mm, "end": v(-9.08, -30.35) * mm});
            skArc(sketch, "E45.5.0.3", {"start": v(9.45, -30.35) * mm, "mid": v(10.56, -29.23) * mm, "end": v(9.45, -28.11) * mm});
            skLineSegment(sketch, "E45.6.0.0", {"start": v(-9.07, -31.9) * mm, "end": v(9.45, -31.9) * mm});
            skLineSegment(sketch, "E45.6.0.1", {"start": v(-9.07, -34.13) * mm, "end": v(9.45, -34.13) * mm});
            skArc(sketch, "E45.6.0.2", {"start": v(-9.07, -31.9) * mm, "mid": v(-10.2, -33.01) * mm, "end": v(-9.07, -34.13) * mm});
            skArc(sketch, "E45.6.0.3", {"start": v(9.45, -34.13) * mm, "mid": v(10.57, -33.01) * mm, "end": v(9.45, -31.9) * mm});
            skLineSegment(sketch, "E45.7.0.0", {"start": v(-9.07, -35.68) * mm, "end": v(9.46, -35.68) * mm});
            skLineSegment(sketch, "E45.7.0.1", {"start": v(-9.07, -37.92) * mm, "end": v(9.46, -37.92) * mm});
            skArc(sketch, "E45.7.0.2", {"start": v(-9.07, -35.68) * mm, "mid": v(-10.18, -36.8) * mm, "end": v(-9.07, -37.92) * mm});
            skArc(sketch, "E45.7.0.3", {"start": v(9.46, -37.92) * mm, "mid": v(10.58, -36.8) * mm, "end": v(9.46, -35.68) * mm});
            skLineSegment(sketch, "E45.direction1", {"start": v(-9.11, -9.19) * mm, "end": v(-9.1, -12.97) * mm, "construction": true});
            skLineSegment(sketch, "E46.bottom", {"start": v(-9.3, -57.25) * mm, "end": v(9.23, -57.25) * mm});
            skLineSegment(sketch, "E46.top", {"start": v(-9.3, -59.48) * mm, "end": v(9.23, -59.48) * mm});
            skArc(sketch, "E47", {"start": v(-9.3, -57.25) * mm, "mid": v(-10.41, -58.36) * mm, "end": v(-9.3, -59.48) * mm});
            skArc(sketch, "E48", {"start": v(9.23, -59.48) * mm, "mid": v(10.35, -58.36) * mm, "end": v(9.23, -57.25) * mm});
            skLineSegment(sketch, "E49.1.0.0", {"start": v(-9.29, -61.03) * mm, "end": v(9.24, -61.03) * mm});
            skLineSegment(sketch, "E49.1.0.1", {"start": v(-9.29, -63.26) * mm, "end": v(9.24, -63.26) * mm});
            skArc(sketch, "E49.1.0.2", {"start": v(-9.29, -61.03) * mm, "mid": v(-10.4, -62.15) * mm, "end": v(-9.29, -63.26) * mm});
            skArc(sketch, "E49.1.0.3", {"start": v(9.24, -63.26) * mm, "mid": v(10.36, -62.15) * mm, "end": v(9.24, -61.03) * mm});
            skLineSegment(sketch, "E49.2.0.0", {"start": v(-9.28, -64.81) * mm, "end": v(9.25, -64.81) * mm});
            skLineSegment(sketch, "E49.2.0.1", {"start": v(-9.28, -67.05) * mm, "end": v(9.25, -67.05) * mm});
            skArc(sketch, "E49.2.0.2", {"start": v(-9.28, -64.81) * mm, "mid": v(-10.4, -65.93) * mm, "end": v(-9.28, -67.05) * mm});
            skArc(sketch, "E49.2.0.3", {"start": v(9.25, -67.05) * mm, "mid": v(10.36, -65.93) * mm, "end": v(9.25, -64.81) * mm});
            skLineSegment(sketch, "E49.3.0.0", {"start": v(-9.27, -68.6) * mm, "end": v(9.25, -68.6) * mm});
            skLineSegment(sketch, "E49.3.0.1", {"start": v(-9.27, -70.83) * mm, "end": v(9.25, -70.83) * mm});
            skArc(sketch, "E49.3.0.2", {"start": v(-9.27, -68.6) * mm, "mid": v(-10.4, -69.72) * mm, "end": v(-9.27, -70.83) * mm});
            skArc(sketch, "E49.3.0.3", {"start": v(9.25, -70.83) * mm, "mid": v(10.37, -69.72) * mm, "end": v(9.25, -68.6) * mm});
            skLineSegment(sketch, "E49.4.0.0", {"start": v(-9.27, -72.38) * mm, "end": v(9.26, -72.38) * mm});
            skLineSegment(sketch, "E49.4.0.1", {"start": v(-9.27, -74.62) * mm, "end": v(9.26, -74.62) * mm});
            skArc(sketch, "E49.4.0.2", {"start": v(-9.27, -72.38) * mm, "mid": v(-10.39, -73.5) * mm, "end": v(-9.27, -74.62) * mm});
            skArc(sketch, "E49.4.0.3", {"start": v(9.26, -74.62) * mm, "mid": v(10.38, -73.5) * mm, "end": v(9.26, -72.38) * mm});
            skLineSegment(sketch, "E49.5.0.0", {"start": v(-9.26, -76.17) * mm, "end": v(9.27, -76.17) * mm});
            skLineSegment(sketch, "E49.5.0.1", {"start": v(-9.26, -78.4) * mm, "end": v(9.27, -78.4) * mm});
            skArc(sketch, "E49.5.0.2", {"start": v(-9.26, -76.17) * mm, "mid": v(-10.38, -77.29) * mm, "end": v(-9.26, -78.4) * mm});
            skArc(sketch, "E49.5.0.3", {"start": v(9.27, -78.4) * mm, "mid": v(10.38, -77.29) * mm, "end": v(9.27, -76.17) * mm});
            skLineSegment(sketch, "E49.6.0.0", {"start": v(-9.25, -79.95) * mm, "end": v(9.27, -79.95) * mm});
            skLineSegment(sketch, "E49.6.0.1", {"start": v(-9.25, -82.19) * mm, "end": v(9.27, -82.19) * mm});
            skArc(sketch, "E49.6.0.2", {"start": v(-9.25, -79.95) * mm, "mid": v(-10.37, -81.07) * mm, "end": v(-9.25, -82.19) * mm});
            skArc(sketch, "E49.6.0.3", {"start": v(9.27, -82.19) * mm, "mid": v(10.4, -81.07) * mm, "end": v(9.27, -79.95) * mm});
            skLineSegment(sketch, "E49.7.0.0", {"start": v(-9.25, -83.74) * mm, "end": v(9.28, -83.74) * mm});
            skLineSegment(sketch, "E49.7.0.1", {"start": v(-9.25, -85.97) * mm, "end": v(9.28, -85.97) * mm});
            skArc(sketch, "E49.7.0.2", {"start": v(-9.25, -83.74) * mm, "mid": v(-10.37, -84.85) * mm, "end": v(-9.25, -85.97) * mm});
            skArc(sketch, "E49.7.0.3", {"start": v(9.28, -85.97) * mm, "mid": v(10.4, -84.85) * mm, "end": v(9.28, -83.74) * mm});
            skLineSegment(sketch, "E49.direction1", {"start": v(-9.3, -57.25) * mm, "end": v(-9.29, -61.03) * mm, "construction": true});
            skSolve(sketch);
        }
        {
            var Q0;
            Q0=makeQuery(id+"F15.imprint","IMPRINT",FACE,{"disambiguationData":[TD([[makeQuery(id+"F15.imprint","IMPRINT",EDGE,{"derivedFrom":sQuery(id+"F15.wireOp",EDGE,"E42.bottom")}),-1.0]])]});
            var Q1;
            Q1=makeQuery(id+"F15.imprint","IMPRINT",FACE,{"disambiguationData":[TD([[makeQuery(id+"F15.imprint","IMPRINT",EDGE,{"derivedFrom":sQuery(id+"F15.wireOp",EDGE,"E45.1.0.0")}),-1.0]])]});
            var Q2;
            Q2=makeQuery(id+"F15.imprint","IMPRINT",FACE,{"disambiguationData":[TD([[makeQuery(id+"F15.imprint","IMPRINT",EDGE,{"derivedFrom":sQuery(id+"F15.wireOp",EDGE,"E45.2.0.0")}),-1.0]])]});
            var Q3;
            Q3=makeQuery(id+"F15.imprint","IMPRINT",FACE,{"disambiguationData":[TD([[makeQuery(id+"F15.imprint","IMPRINT",EDGE,{"derivedFrom":sQuery(id+"F15.wireOp",EDGE,"E45.3.0.0")}),-1.0]])]});
            var Q4;
            Q4=makeQuery(id+"F15.imprint","IMPRINT",FACE,{"disambiguationData":[TD([[makeQuery(id+"F15.imprint","IMPRINT",EDGE,{"derivedFrom":sQuery(id+"F15.wireOp",EDGE,"E45.4.0.0")}),-1.0]])]});
            var Q5;
            Q5=makeQuery(id+"F15.imprint","IMPRINT",FACE,{"disambiguationData":[TD([[makeQuery(id+"F15.imprint","IMPRINT",EDGE,{"derivedFrom":sQuery(id+"F15.wireOp",EDGE,"E45.5.0.0")}),-1.0]])]});
            var Q6;
            Q6=makeQuery(id+"F15.imprint","IMPRINT",FACE,{"disambiguationData":[TD([[makeQuery(id+"F15.imprint","IMPRINT",EDGE,{"derivedFrom":sQuery(id+"F15.wireOp",EDGE,"E45.6.0.0")}),-1.0]])]});
            var Q7;
            Q7=makeQuery(id+"F15.imprint","IMPRINT",FACE,{"disambiguationData":[TD([[makeQuery(id+"F15.imprint","IMPRINT",EDGE,{"derivedFrom":sQuery(id+"F15.wireOp",EDGE,"E45.7.0.0")}),-1.0]])]});
            var Q8;
            Q8=makeQuery(id+"F15.imprint","IMPRINT",FACE,{"disambiguationData":[TD([[makeQuery(id+"F15.imprint","IMPRINT",EDGE,{"derivedFrom":sQuery(id+"F15.wireOp",EDGE,"E46.bottom")}),-1.0]])]});
            var Q9;
            Q9=makeQuery(id+"F15.imprint","IMPRINT",FACE,{"disambiguationData":[TD([[makeQuery(id+"F15.imprint","IMPRINT",EDGE,{"derivedFrom":sQuery(id+"F15.wireOp",EDGE,"E49.1.0.0")}),-1.0]])]});
            var Q10;
            Q10=makeQuery(id+"F15.imprint","IMPRINT",FACE,{"disambiguationData":[TD([[makeQuery(id+"F15.imprint","IMPRINT",EDGE,{"derivedFrom":sQuery(id+"F15.wireOp",EDGE,"E49.2.0.0")}),-1.0]])]});
            var Q11;
            Q11=makeQuery(id+"F15.imprint","IMPRINT",FACE,{"disambiguationData":[TD([[makeQuery(id+"F15.imprint","IMPRINT",EDGE,{"derivedFrom":sQuery(id+"F15.wireOp",EDGE,"E49.3.0.0")}),-1.0]])]});
            var Q12;
            Q12=makeQuery(id+"F15.imprint","IMPRINT",FACE,{"disambiguationData":[TD([[makeQuery(id+"F15.imprint","IMPRINT",EDGE,{"derivedFrom":sQuery(id+"F15.wireOp",EDGE,"E49.4.0.0")}),-1.0]])]});
            var Q13;
            Q13=makeQuery(id+"F15.imprint","IMPRINT",FACE,{"disambiguationData":[TD([[makeQuery(id+"F15.imprint","IMPRINT",EDGE,{"derivedFrom":sQuery(id+"F15.wireOp",EDGE,"E49.5.0.0")}),-1.0]])]});
            var Q14;
            Q14=makeQuery(id+"F15.imprint","IMPRINT",FACE,{"disambiguationData":[TD([[makeQuery(id+"F15.imprint","IMPRINT",EDGE,{"derivedFrom":sQuery(id+"F15.wireOp",EDGE,"E49.6.0.0")}),-1.0]])]});
            var Q15;
            Q15=makeQuery(id+"F15.imprint","IMPRINT",FACE,{"disambiguationData":[TD([[makeQuery(id+"F15.imprint","IMPRINT",EDGE,{"derivedFrom":sQuery(id+"F15.wireOp",EDGE,"E49.7.0.0")}),-1.0]])]});
            extrude(context, id + "F16", {"entities" : qUnion([Q0, Q1, Q2, Q3, Q4, Q5, Q6, Q7, Q8, Q9, Q10, Q11, Q12, Q13, Q14, Q15]), "operationType" : NewBodyOperationType.REMOVE, "oppositeDirection" : true, "depth" : 25.4 * mm});
        }
        {
            var Q0;
            Q0=makeQuery(id+"F1.opExtrude","SWEPT_FACE",FACE,{"disambiguationData":[OSD([sQuery(id+"F0.wireOp",EDGE,"E0.right")])]});
            var sketch = newSketch(context, id + "F17", { "sketchPlane" : qUnion([Q0])});
            skLineSegment(sketch, "E50.bottom", {"start": v(-8.92, -9.61) * mm, "end": v(9.61, -9.61) * mm});
            skLineSegment(sketch, "E50.top", {"start": v(-8.92, -11.85) * mm, "end": v(9.61, -11.85) * mm});
            skArc(sketch, "E51", {"start": v(-8.92, -9.61) * mm, "mid": v(-10.03, -10.73) * mm, "end": v(-8.92, -11.85) * mm});
            skArc(sketch, "E52", {"start": v(9.61, -11.85) * mm, "mid": v(10.73, -10.73) * mm, "end": v(9.61, -9.61) * mm});
            skLineSegment(sketch, "E53.1.0.0", {"start": v(-8.9, -13.4) * mm, "end": v(9.62, -13.4) * mm});
            skLineSegment(sketch, "E53.1.0.1", {"start": v(-8.9, -15.63) * mm, "end": v(9.62, -15.63) * mm});
            skArc(sketch, "E53.1.0.2", {"start": v(-8.9, -13.4) * mm, "mid": v(-10.03, -14.51) * mm, "end": v(-8.9, -15.63) * mm});
            skArc(sketch, "E53.1.0.3", {"start": v(9.62, -15.63) * mm, "mid": v(10.74, -14.51) * mm, "end": v(9.62, -13.4) * mm});
            skLineSegment(sketch, "E53.2.0.0", {"start": v(-8.9, -17.18) * mm, "end": v(9.63, -17.18) * mm});
            skLineSegment(sketch, "E53.2.0.1", {"start": v(-8.9, -19.42) * mm, "end": v(9.63, -19.42) * mm});
            skArc(sketch, "E53.2.0.2", {"start": v(-8.9, -17.18) * mm, "mid": v(-10.02, -18.3) * mm, "end": v(-8.9, -19.42) * mm});
            skArc(sketch, "E53.2.0.3", {"start": v(9.63, -19.42) * mm, "mid": v(10.74, -18.3) * mm, "end": v(9.63, -17.18) * mm});
            skLineSegment(sketch, "E53.3.0.0", {"start": v(-8.9, -20.96) * mm, "end": v(9.63, -20.96) * mm});
            skLineSegment(sketch, "E53.3.0.1", {"start": v(-8.9, -23.2) * mm, "end": v(9.63, -23.2) * mm});
            skArc(sketch, "E53.3.0.2", {"start": v(-8.9, -20.96) * mm, "mid": v(-10.01, -22.08) * mm, "end": v(-8.9, -23.2) * mm});
            skArc(sketch, "E53.3.0.3", {"start": v(9.63, -23.2) * mm, "mid": v(10.75, -22.08) * mm, "end": v(9.63, -20.96) * mm});
            skLineSegment(sketch, "E53.4.0.0", {"start": v(-8.89, -24.75) * mm, "end": v(9.64, -24.75) * mm});
            skLineSegment(sketch, "E53.4.0.1", {"start": v(-8.89, -26.98) * mm, "end": v(9.64, -26.98) * mm});
            skArc(sketch, "E53.4.0.2", {"start": v(-8.89, -24.75) * mm, "mid": v(-10, -25.87) * mm, "end": v(-8.89, -26.98) * mm});
            skArc(sketch, "E53.4.0.3", {"start": v(9.64, -26.98) * mm, "mid": v(10.76, -25.87) * mm, "end": v(9.64, -24.75) * mm});
            skLineSegment(sketch, "E53.5.0.0", {"start": v(-8.88, -28.53) * mm, "end": v(9.65, -28.53) * mm});
            skLineSegment(sketch, "E53.5.0.1", {"start": v(-8.88, -30.77) * mm, "end": v(9.65, -30.77) * mm});
            skArc(sketch, "E53.5.0.2", {"start": v(-8.88, -28.53) * mm, "mid": v(-10, -29.65) * mm, "end": v(-8.88, -30.77) * mm});
            skArc(sketch, "E53.5.0.3", {"start": v(9.65, -30.77) * mm, "mid": v(10.76, -29.65) * mm, "end": v(9.65, -28.53) * mm});
            skLineSegment(sketch, "E53.6.0.0", {"start": v(-8.88, -32.32) * mm, "end": v(9.65, -32.32) * mm});
            skLineSegment(sketch, "E53.6.0.1", {"start": v(-8.88, -34.55) * mm, "end": v(9.65, -34.55) * mm});
            skArc(sketch, "E53.6.0.2", {"start": v(-8.88, -32.32) * mm, "mid": v(-10, -33.44) * mm, "end": v(-8.88, -34.55) * mm});
            skArc(sketch, "E53.6.0.3", {"start": v(9.65, -34.55) * mm, "mid": v(10.77, -33.44) * mm, "end": v(9.65, -32.32) * mm});
            skLineSegment(sketch, "E53.7.0.0", {"start": v(-8.87, -36.1) * mm, "end": v(9.66, -36.1) * mm});
            skLineSegment(sketch, "E53.7.0.1", {"start": v(-8.87, -38.34) * mm, "end": v(9.66, -38.34) * mm});
            skArc(sketch, "E53.7.0.2", {"start": v(-8.87, -36.1) * mm, "mid": v(-9.99, -37.22) * mm, "end": v(-8.87, -38.34) * mm});
            skArc(sketch, "E53.7.0.3", {"start": v(9.66, -38.34) * mm, "mid": v(10.78, -37.22) * mm, "end": v(9.66, -36.1) * mm});
            skLineSegment(sketch, "E53.direction1", {"start": v(-8.92, -9.61) * mm, "end": v(-8.9, -13.4) * mm, "construction": true});
            skLineSegment(sketch, "E54.bottom", {"start": v(-9.1, -57.67) * mm, "end": v(9.43, -57.67) * mm});
            skLineSegment(sketch, "E54.top", {"start": v(-9.1, -59.9) * mm, "end": v(9.43, -59.9) * mm});
            skArc(sketch, "E55", {"start": v(-9.1, -57.67) * mm, "mid": v(-10.21, -58.79) * mm, "end": v(-9.1, -59.9) * mm});
            skArc(sketch, "E56", {"start": v(9.43, -59.9) * mm, "mid": v(10.55, -58.79) * mm, "end": v(9.43, -57.67) * mm});
            skLineSegment(sketch, "E57.1.0.0", {"start": v(-9.09, -61.45) * mm, "end": v(9.44, -61.45) * mm});
            skLineSegment(sketch, "E57.1.0.1", {"start": v(-9.09, -63.69) * mm, "end": v(9.44, -63.69) * mm});
            skArc(sketch, "E57.1.0.2", {"start": v(-9.09, -61.45) * mm, "mid": v(-10.2, -62.57) * mm, "end": v(-9.09, -63.69) * mm});
            skArc(sketch, "E57.1.0.3", {"start": v(9.44, -63.69) * mm, "mid": v(10.56, -62.57) * mm, "end": v(9.44, -61.45) * mm});
            skLineSegment(sketch, "E57.2.0.0", {"start": v(-9.08, -65.24) * mm, "end": v(9.44, -65.24) * mm});
            skLineSegment(sketch, "E57.2.0.1", {"start": v(-9.08, -67.47) * mm, "end": v(9.44, -67.47) * mm});
            skArc(sketch, "E57.2.0.2", {"start": v(-9.08, -65.24) * mm, "mid": v(-10.2, -66.35) * mm, "end": v(-9.08, -67.47) * mm});
            skArc(sketch, "E57.2.0.3", {"start": v(9.44, -67.47) * mm, "mid": v(10.56, -66.35) * mm, "end": v(9.44, -65.24) * mm});
            skLineSegment(sketch, "E57.3.0.0", {"start": v(-9.08, -69.02) * mm, "end": v(9.45, -69.02) * mm});
            skLineSegment(sketch, "E57.3.0.1", {"start": v(-9.08, -71.26) * mm, "end": v(9.45, -71.26) * mm});
            skArc(sketch, "E57.3.0.2", {"start": v(-9.08, -69.02) * mm, "mid": v(-10.2, -70.14) * mm, "end": v(-9.08, -71.26) * mm});
            skArc(sketch, "E57.3.0.3", {"start": v(9.45, -71.26) * mm, "mid": v(10.57, -70.14) * mm, "end": v(9.45, -69.02) * mm});
            skLineSegment(sketch, "E57.4.0.0", {"start": v(-9.07, -72.8) * mm, "end": v(9.46, -72.8) * mm});
            skLineSegment(sketch, "E57.4.0.1", {"start": v(-9.07, -75.04) * mm, "end": v(9.46, -75.04) * mm});
            skArc(sketch, "E57.4.0.2", {"start": v(-9.07, -72.8) * mm, "mid": v(-10.19, -73.92) * mm, "end": v(-9.07, -75.04) * mm});
            skArc(sketch, "E57.4.0.3", {"start": v(9.46, -75.04) * mm, "mid": v(10.58, -73.92) * mm, "end": v(9.46, -72.8) * mm});
            skLineSegment(sketch, "E57.5.0.0", {"start": v(-9.06, -76.6) * mm, "end": v(9.46, -76.6) * mm});
            skLineSegment(sketch, "E57.5.0.1", {"start": v(-9.06, -78.83) * mm, "end": v(9.46, -78.83) * mm});
            skArc(sketch, "E57.5.0.2", {"start": v(-9.06, -76.6) * mm, "mid": v(-10.18, -77.7) * mm, "end": v(-9.06, -78.83) * mm});
            skArc(sketch, "E57.5.0.3", {"start": v(9.46, -78.83) * mm, "mid": v(10.58, -77.7) * mm, "end": v(9.46, -76.6) * mm});
            skLineSegment(sketch, "E57.6.0.0", {"start": v(-9.06, -80.38) * mm, "end": v(9.47, -80.38) * mm});
            skLineSegment(sketch, "E57.6.0.1", {"start": v(-9.06, -82.61) * mm, "end": v(9.47, -82.61) * mm});
            skArc(sketch, "E57.6.0.2", {"start": v(-9.06, -80.38) * mm, "mid": v(-10.17, -81.5) * mm, "end": v(-9.06, -82.61) * mm});
            skArc(sketch, "E57.6.0.3", {"start": v(9.47, -82.61) * mm, "mid": v(10.59, -81.5) * mm, "end": v(9.47, -80.38) * mm});
            skLineSegment(sketch, "E57.7.0.0", {"start": v(-9.05, -84.16) * mm, "end": v(9.48, -84.16) * mm});
            skLineSegment(sketch, "E57.7.0.1", {"start": v(-9.05, -86.4) * mm, "end": v(9.48, -86.4) * mm});
            skArc(sketch, "E57.7.0.2", {"start": v(-9.05, -84.16) * mm, "mid": v(-10.17, -85.28) * mm, "end": v(-9.05, -86.4) * mm});
            skArc(sketch, "E57.7.0.3", {"start": v(9.48, -86.4) * mm, "mid": v(10.6, -85.28) * mm, "end": v(9.48, -84.16) * mm});
            skLineSegment(sketch, "E57.direction1", {"start": v(-9.1, -57.67) * mm, "end": v(-9.09, -61.45) * mm, "construction": true});
            skSolve(sketch);
        }
        {
            var Q0;
            Q0=makeQuery(id+"F17.imprint","IMPRINT",FACE,{"disambiguationData":[TD([[makeQuery(id+"F17.imprint","IMPRINT",EDGE,{"derivedFrom":sQuery(id+"F17.wireOp",EDGE,"E50.bottom")}),-1.0]])]});
            var Q1;
            Q1=makeQuery(id+"F17.imprint","IMPRINT",FACE,{"disambiguationData":[TD([[makeQuery(id+"F17.imprint","IMPRINT",EDGE,{"derivedFrom":sQuery(id+"F17.wireOp",EDGE,"E53.1.0.0")}),-1.0]])]});
            var Q2;
            Q2=makeQuery(id+"F17.imprint","IMPRINT",FACE,{"disambiguationData":[TD([[makeQuery(id+"F17.imprint","IMPRINT",EDGE,{"derivedFrom":sQuery(id+"F17.wireOp",EDGE,"E53.2.0.0")}),-1.0]])]});
            var Q3;
            Q3=makeQuery(id+"F17.imprint","IMPRINT",FACE,{"disambiguationData":[TD([[makeQuery(id+"F17.imprint","IMPRINT",EDGE,{"derivedFrom":sQuery(id+"F17.wireOp",EDGE,"E53.3.0.0")}),-1.0]])]});
            var Q4;
            Q4=makeQuery(id+"F17.imprint","IMPRINT",FACE,{"disambiguationData":[TD([[makeQuery(id+"F17.imprint","IMPRINT",EDGE,{"derivedFrom":sQuery(id+"F17.wireOp",EDGE,"E53.4.0.0")}),-1.0]])]});
            var Q5;
            Q5=makeQuery(id+"F17.imprint","IMPRINT",FACE,{"disambiguationData":[TD([[makeQuery(id+"F17.imprint","IMPRINT",EDGE,{"derivedFrom":sQuery(id+"F17.wireOp",EDGE,"E53.5.0.0")}),-1.0]])]});
            var Q6;
            Q6=makeQuery(id+"F17.imprint","IMPRINT",FACE,{"disambiguationData":[TD([[makeQuery(id+"F17.imprint","IMPRINT",EDGE,{"derivedFrom":sQuery(id+"F17.wireOp",EDGE,"E53.6.0.0")}),-1.0]])]});
            var Q7;
            Q7=makeQuery(id+"F17.imprint","IMPRINT",FACE,{"disambiguationData":[TD([[makeQuery(id+"F17.imprint","IMPRINT",EDGE,{"derivedFrom":sQuery(id+"F17.wireOp",EDGE,"E53.7.0.0")}),-1.0]])]});
            var Q8;
            Q8=makeQuery(id+"F17.imprint","IMPRINT",FACE,{"disambiguationData":[TD([[makeQuery(id+"F17.imprint","IMPRINT",EDGE,{"derivedFrom":sQuery(id+"F17.wireOp",EDGE,"E54.bottom")}),-1.0]])]});
            var Q9;
            Q9=makeQuery(id+"F17.imprint","IMPRINT",FACE,{"disambiguationData":[TD([[makeQuery(id+"F17.imprint","IMPRINT",EDGE,{"derivedFrom":sQuery(id+"F17.wireOp",EDGE,"E57.1.0.0")}),-1.0]])]});
            var Q10;
            Q10=makeQuery(id+"F17.imprint","IMPRINT",FACE,{"disambiguationData":[TD([[makeQuery(id+"F17.imprint","IMPRINT",EDGE,{"derivedFrom":sQuery(id+"F17.wireOp",EDGE,"E57.2.0.0")}),-1.0]])]});
            var Q11;
            Q11=makeQuery(id+"F17.imprint","IMPRINT",FACE,{"disambiguationData":[TD([[makeQuery(id+"F17.imprint","IMPRINT",EDGE,{"derivedFrom":sQuery(id+"F17.wireOp",EDGE,"E57.3.0.0")}),-1.0]])]});
            var Q12;
            Q12=makeQuery(id+"F17.imprint","IMPRINT",FACE,{"disambiguationData":[TD([[makeQuery(id+"F17.imprint","IMPRINT",EDGE,{"derivedFrom":sQuery(id+"F17.wireOp",EDGE,"E57.4.0.0")}),-1.0]])]});
            var Q13;
            Q13=makeQuery(id+"F17.imprint","IMPRINT",FACE,{"disambiguationData":[TD([[makeQuery(id+"F17.imprint","IMPRINT",EDGE,{"derivedFrom":sQuery(id+"F17.wireOp",EDGE,"E57.5.0.0")}),-1.0]])]});
            var Q14;
            Q14=makeQuery(id+"F17.imprint","IMPRINT",FACE,{"disambiguationData":[TD([[makeQuery(id+"F17.imprint","IMPRINT",EDGE,{"derivedFrom":sQuery(id+"F17.wireOp",EDGE,"E57.6.0.0")}),-1.0]])]});
            var Q15;
            Q15=makeQuery(id+"F17.imprint","IMPRINT",FACE,{"disambiguationData":[TD([[makeQuery(id+"F17.imprint","IMPRINT",EDGE,{"derivedFrom":sQuery(id+"F17.wireOp",EDGE,"E57.7.0.0")}),-1.0]])]});
            extrude(context, id + "F18", {"entities" : qUnion([Q0, Q1, Q2, Q3, Q4, Q5, Q6, Q7, Q8, Q9, Q10, Q11, Q12, Q13, Q14, Q15]), "operationType" : NewBodyOperationType.REMOVE, "oppositeDirection" : true, "depth" : 25.4 * mm});
        }
        {
            var Q0;
            {var subQ0=sQuery(id+"F0.wireOp",EDGE,"E1.left");var subQ1=sQuery(id+"F0.wireOp",EDGE,"E1.top");var subQ3=sQuery(id+"F3.wireOp",EDGE,"E36.left");Q0=makeQuery(id+"F6.boolean.opBoolean","SPLIT",EDGE,{"disambiguationData":[TD([makeQuery(id+"F6.opExtrude","SWEPT_FACE",FACE,{"disambiguationData":[OSD([sQuery(id+"F5.wireOp",EDGE,"E37.bottom")])]})])],"derivedFrom":makeQuery(id+"F4.boolean.opBoolean","MERGE",EDGE,{"derivedFrom":[makeQuery(id+"F2.opExtrude","SWEPT_EDGE",EDGE,{"disambiguationData":[OSD([subQ1,subQ0])]}),makeQuery(id+"F4.opExtrude","CAP_EDGE",EDGE,{"disambiguationData":[OSD([subQ3])],"isStart":true})]})});}
            var Q1;
            {var subQ0=sQuery(id+"F3.wireOp",EDGE,"E36.left");var subQ1=sQuery(id+"F0.wireOp",EDGE,"E1.left");var subQ2=sQuery(id+"F0.wireOp",EDGE,"E1.top");Q1=makeQuery(id+"F6.boolean.opBoolean","SPLIT",EDGE,{"disambiguationData":[TD([makeQuery(id+"F6.opExtrude","SWEPT_FACE",FACE,{"disambiguationData":[OSD([sQuery(id+"F5.wireOp",EDGE,"E38.1.0.0")])]})])],"derivedFrom":makeQuery(id+"F4.boolean.opBoolean","MERGE",EDGE,{"derivedFrom":[makeQuery(id+"F2.opExtrude","SWEPT_EDGE",EDGE,{"disambiguationData":[OSD([subQ2,subQ1])]}),makeQuery(id+"F4.opExtrude","CAP_EDGE",EDGE,{"disambiguationData":[OSD([subQ0])],"isStart":true})]})});}
            var Q2;
            {var subQ0=sQuery(id+"F3.wireOp",EDGE,"E36.left");var subQ1=sQuery(id+"F0.wireOp",EDGE,"E1.left");var subQ2=sQuery(id+"F0.wireOp",EDGE,"E1.top");Q2=makeQuery(id+"F6.boolean.opBoolean","SPLIT",EDGE,{"disambiguationData":[TD([makeQuery(id+"F6.opExtrude","SWEPT_FACE",FACE,{"disambiguationData":[OSD([sQuery(id+"F5.wireOp",EDGE,"E38.2.0.0")])]})])],"derivedFrom":makeQuery(id+"F4.boolean.opBoolean","MERGE",EDGE,{"derivedFrom":[makeQuery(id+"F2.opExtrude","SWEPT_EDGE",EDGE,{"disambiguationData":[OSD([subQ2,subQ1])]}),makeQuery(id+"F4.opExtrude","CAP_EDGE",EDGE,{"disambiguationData":[OSD([subQ0])],"isStart":true})]})});}
            var Q3;
            {var subQ0=sQuery(id+"F3.wireOp",EDGE,"E36.left");var subQ1=sQuery(id+"F0.wireOp",EDGE,"E1.left");var subQ2=sQuery(id+"F0.wireOp",EDGE,"E1.top");Q3=makeQuery(id+"F6.boolean.opBoolean","SPLIT",EDGE,{"disambiguationData":[TD([makeQuery(id+"F6.opExtrude","SWEPT_FACE",FACE,{"disambiguationData":[OSD([sQuery(id+"F5.wireOp",EDGE,"E38.3.0.0")])]})])],"derivedFrom":makeQuery(id+"F4.boolean.opBoolean","MERGE",EDGE,{"derivedFrom":[makeQuery(id+"F2.opExtrude","SWEPT_EDGE",EDGE,{"disambiguationData":[OSD([subQ2,subQ1])]}),makeQuery(id+"F4.opExtrude","CAP_EDGE",EDGE,{"disambiguationData":[OSD([subQ0])],"isStart":true})]})});}
            var Q4;
            {var subQ0=sQuery(id+"F3.wireOp",EDGE,"E36.left");var subQ1=sQuery(id+"F0.wireOp",EDGE,"E1.left");var subQ2=sQuery(id+"F0.wireOp",EDGE,"E1.top");Q4=makeQuery(id+"F6.boolean.opBoolean","SPLIT",EDGE,{"disambiguationData":[TD([makeQuery(id+"F6.opExtrude","SWEPT_FACE",FACE,{"disambiguationData":[OSD([sQuery(id+"F5.wireOp",EDGE,"E37.top")])]})])],"derivedFrom":makeQuery(id+"F4.boolean.opBoolean","MERGE",EDGE,{"derivedFrom":[makeQuery(id+"F2.opExtrude","SWEPT_EDGE",EDGE,{"disambiguationData":[OSD([subQ2,subQ1])]}),makeQuery(id+"F4.opExtrude","CAP_EDGE",EDGE,{"disambiguationData":[OSD([subQ0])],"isStart":true})]})});}
            var Q5;
            {var subQ0=sQuery(id+"F3.wireOp",EDGE,"E36.left");var subQ1=sQuery(id+"F0.wireOp",EDGE,"E1.left");var subQ2=sQuery(id+"F0.wireOp",EDGE,"E1.top");Q5=makeQuery(id+"F6.boolean.opBoolean","SPLIT",EDGE,{"disambiguationData":[TD([makeQuery(id+"F6.opExtrude","SWEPT_FACE",FACE,{"disambiguationData":[OSD([sQuery(id+"F5.wireOp",EDGE,"E38.4.0.0")])]})])],"derivedFrom":makeQuery(id+"F4.boolean.opBoolean","MERGE",EDGE,{"derivedFrom":[makeQuery(id+"F2.opExtrude","SWEPT_EDGE",EDGE,{"disambiguationData":[OSD([subQ2,subQ1])]}),makeQuery(id+"F4.opExtrude","CAP_EDGE",EDGE,{"disambiguationData":[OSD([subQ0])],"isStart":true})]})});}
            var Q6;
            {var subQ0=sQuery(id+"F3.wireOp",EDGE,"E36.left");var subQ1=sQuery(id+"F0.wireOp",EDGE,"E1.left");var subQ2=sQuery(id+"F0.wireOp",EDGE,"E1.top");Q6=makeQuery(id+"F6.boolean.opBoolean","SPLIT",EDGE,{"disambiguationData":[TD([makeQuery(id+"F6.opExtrude","SWEPT_FACE",FACE,{"disambiguationData":[OSD([sQuery(id+"F5.wireOp",EDGE,"E38.5.0.0")])]})])],"derivedFrom":makeQuery(id+"F4.boolean.opBoolean","MERGE",EDGE,{"derivedFrom":[makeQuery(id+"F2.opExtrude","SWEPT_EDGE",EDGE,{"disambiguationData":[OSD([subQ2,subQ1])]}),makeQuery(id+"F4.opExtrude","CAP_EDGE",EDGE,{"disambiguationData":[OSD([subQ0])],"isStart":true})]})});}
            var Q7;
            {var subQ0=sQuery(id+"F3.wireOp",EDGE,"E36.left");var subQ1=sQuery(id+"F0.wireOp",EDGE,"E1.left");var subQ2=sQuery(id+"F0.wireOp",EDGE,"E1.top");Q7=makeQuery(id+"F6.boolean.opBoolean","SPLIT",EDGE,{"disambiguationData":[TD([makeQuery(id+"F6.opExtrude","SWEPT_FACE",FACE,{"disambiguationData":[OSD([sQuery(id+"F5.wireOp",EDGE,"E38.6.0.0")])]})])],"derivedFrom":makeQuery(id+"F4.boolean.opBoolean","MERGE",EDGE,{"derivedFrom":[makeQuery(id+"F2.opExtrude","SWEPT_EDGE",EDGE,{"disambiguationData":[OSD([subQ2,subQ1])]}),makeQuery(id+"F4.opExtrude","CAP_EDGE",EDGE,{"disambiguationData":[OSD([subQ0])],"isStart":true})]})});}
            var Q8;
            {var subQ0=sQuery(id+"F3.wireOp",EDGE,"E36.left");var subQ1=sQuery(id+"F0.wireOp",EDGE,"E1.left");var subQ2=sQuery(id+"F0.wireOp",EDGE,"E1.top");Q8=makeQuery(id+"F6.boolean.opBoolean","SPLIT",EDGE,{"disambiguationData":[TD([makeQuery(id+"F6.opExtrude","SWEPT_FACE",FACE,{"disambiguationData":[OSD([sQuery(id+"F5.wireOp",EDGE,"E38.7.0.0")])]})])],"derivedFrom":makeQuery(id+"F4.boolean.opBoolean","MERGE",EDGE,{"derivedFrom":[makeQuery(id+"F2.opExtrude","SWEPT_EDGE",EDGE,{"disambiguationData":[OSD([subQ2,subQ1])]}),makeQuery(id+"F4.opExtrude","CAP_EDGE",EDGE,{"disambiguationData":[OSD([subQ0])],"isStart":true})]})});}
            var Q9;
            {var subQ0=sQuery(id+"F3.wireOp",EDGE,"E36.left");var subQ1=sQuery(id+"F0.wireOp",EDGE,"E1.left");var subQ2=sQuery(id+"F0.wireOp",EDGE,"E1.top");Q9=makeQuery(id+"F6.boolean.opBoolean","SPLIT",EDGE,{"disambiguationData":[TD([makeQuery(id+"F6.opExtrude","SWEPT_FACE",FACE,{"disambiguationData":[OSD([sQuery(id+"F5.wireOp",EDGE,"E38.8.0.0")])]})])],"derivedFrom":makeQuery(id+"F4.boolean.opBoolean","MERGE",EDGE,{"derivedFrom":[makeQuery(id+"F2.opExtrude","SWEPT_EDGE",EDGE,{"disambiguationData":[OSD([subQ2,subQ1])]}),makeQuery(id+"F4.opExtrude","CAP_EDGE",EDGE,{"disambiguationData":[OSD([subQ0])],"isStart":true})]})});}
            var Q10;
            {var subQ0=sQuery(id+"F3.wireOp",EDGE,"E36.left");var subQ1=sQuery(id+"F0.wireOp",EDGE,"E1.left");var subQ2=sQuery(id+"F0.wireOp",EDGE,"E1.top");Q10=makeQuery(id+"F6.boolean.opBoolean","SPLIT",EDGE,{"disambiguationData":[TD([makeQuery(id+"F6.opExtrude","SWEPT_FACE",FACE,{"disambiguationData":[OSD([sQuery(id+"F5.wireOp",EDGE,"E38.9.0.0")])]})])],"derivedFrom":makeQuery(id+"F4.boolean.opBoolean","MERGE",EDGE,{"derivedFrom":[makeQuery(id+"F2.opExtrude","SWEPT_EDGE",EDGE,{"disambiguationData":[OSD([subQ2,subQ1])]}),makeQuery(id+"F4.opExtrude","CAP_EDGE",EDGE,{"disambiguationData":[OSD([subQ0])],"isStart":true})]})});}
            var Q11;
            {var subQ0=sQuery(id+"F3.wireOp",EDGE,"E36.top");var subQ1=sQuery(id+"F3.wireOp",EDGE,"E36.left");var subQ2=sQuery(id+"F0.wireOp",EDGE,"E1.left");var subQ3=sQuery(id+"F0.wireOp",EDGE,"E1.top");Q11=makeQuery(id+"F6.boolean.opBoolean","SPLIT",EDGE,{"disambiguationData":[TD([makeQuery(id+"F4.opExtrude","SWEPT_FACE",FACE,{"disambiguationData":[OSD([subQ0])]})])],"derivedFrom":makeQuery(id+"F4.boolean.opBoolean","MERGE",EDGE,{"derivedFrom":[makeQuery(id+"F2.opExtrude","SWEPT_EDGE",EDGE,{"disambiguationData":[OSD([subQ3,subQ2])]}),makeQuery(id+"F4.opExtrude","CAP_EDGE",EDGE,{"disambiguationData":[OSD([subQ1])],"isStart":true})]})});}
            var Q12;
            Q12=makeQuery(id+"F4.opExtrude","CAP_EDGE",EDGE,{"disambiguationData":[OSD([sQuery(id+"F3.wireOp",EDGE,"E36.right")])],"isStart":true});
            var Q13;
            {var subQ0=sQuery(id+"F0.wireOp",EDGE,"E1.right");var subQ1=sQuery(id+"F0.wireOp",EDGE,"E1.top");Q13=makeQuery(id+"F6.boolean.opBoolean","SPLIT",EDGE,{"disambiguationData":[TD([makeQuery(id+"F6.opExtrude","SWEPT_FACE",FACE,{"disambiguationData":[OSD([sQuery(id+"F5.wireOp",EDGE,"E38.9.0.0")])]})])],"derivedFrom":makeQuery(id+"F2.opExtrude","SWEPT_EDGE",EDGE,{"disambiguationData":[OSD([subQ1,subQ0])]})});}
            var Q14;
            {var subQ0=sQuery(id+"F0.wireOp",EDGE,"E1.top");var subQ1=sQuery(id+"F0.wireOp",EDGE,"E1.right");Q14=makeQuery(id+"F6.boolean.opBoolean","SPLIT",EDGE,{"disambiguationData":[TD([makeQuery(id+"F6.opExtrude","SWEPT_FACE",FACE,{"disambiguationData":[OSD([sQuery(id+"F5.wireOp",EDGE,"E38.8.0.0")])]})])],"derivedFrom":makeQuery(id+"F2.opExtrude","SWEPT_EDGE",EDGE,{"disambiguationData":[OSD([subQ0,subQ1])]})});}
            var Q15;
            {var subQ0=sQuery(id+"F0.wireOp",EDGE,"E1.right");var subQ1=sQuery(id+"F0.wireOp",EDGE,"E1.top");Q15=makeQuery(id+"F6.boolean.opBoolean","SPLIT",EDGE,{"disambiguationData":[TD([makeQuery(id+"F6.opExtrude","SWEPT_FACE",FACE,{"disambiguationData":[OSD([sQuery(id+"F5.wireOp",EDGE,"E38.7.0.0")])]})])],"derivedFrom":makeQuery(id+"F2.opExtrude","SWEPT_EDGE",EDGE,{"disambiguationData":[OSD([subQ1,subQ0])]})});}
            var Q16;
            {var subQ0=sQuery(id+"F0.wireOp",EDGE,"E1.right");var subQ1=sQuery(id+"F0.wireOp",EDGE,"E1.top");Q16=makeQuery(id+"F6.boolean.opBoolean","SPLIT",EDGE,{"disambiguationData":[TD([makeQuery(id+"F6.opExtrude","SWEPT_FACE",FACE,{"disambiguationData":[OSD([sQuery(id+"F5.wireOp",EDGE,"E38.6.0.0")])]})])],"derivedFrom":makeQuery(id+"F2.opExtrude","SWEPT_EDGE",EDGE,{"disambiguationData":[OSD([subQ1,subQ0])]})});}
            var Q17;
            {var subQ0=sQuery(id+"F0.wireOp",EDGE,"E1.right");var subQ1=sQuery(id+"F0.wireOp",EDGE,"E1.top");Q17=makeQuery(id+"F6.boolean.opBoolean","SPLIT",EDGE,{"disambiguationData":[TD([makeQuery(id+"F6.opExtrude","SWEPT_FACE",FACE,{"disambiguationData":[OSD([sQuery(id+"F5.wireOp",EDGE,"E38.5.0.0")])]})])],"derivedFrom":makeQuery(id+"F2.opExtrude","SWEPT_EDGE",EDGE,{"disambiguationData":[OSD([subQ1,subQ0])]})});}
            var Q18;
            {var subQ0=sQuery(id+"F0.wireOp",EDGE,"E1.right");var subQ1=sQuery(id+"F0.wireOp",EDGE,"E1.top");Q18=makeQuery(id+"F6.boolean.opBoolean","SPLIT",EDGE,{"disambiguationData":[TD([makeQuery(id+"F6.opExtrude","SWEPT_FACE",FACE,{"disambiguationData":[OSD([sQuery(id+"F5.wireOp",EDGE,"E38.4.0.0")])]})])],"derivedFrom":makeQuery(id+"F2.opExtrude","SWEPT_EDGE",EDGE,{"disambiguationData":[OSD([subQ1,subQ0])]})});}
            var Q19;
            {var subQ0=sQuery(id+"F0.wireOp",EDGE,"E1.right");var subQ1=sQuery(id+"F0.wireOp",EDGE,"E1.top");Q19=makeQuery(id+"F6.boolean.opBoolean","SPLIT",EDGE,{"disambiguationData":[TD([makeQuery(id+"F6.opExtrude","SWEPT_FACE",FACE,{"disambiguationData":[OSD([sQuery(id+"F5.wireOp",EDGE,"E38.3.0.0")])]})])],"derivedFrom":makeQuery(id+"F2.opExtrude","SWEPT_EDGE",EDGE,{"disambiguationData":[OSD([subQ1,subQ0])]})});}
            var Q20;
            {var subQ0=sQuery(id+"F0.wireOp",EDGE,"E1.right");var subQ1=sQuery(id+"F0.wireOp",EDGE,"E1.top");Q20=makeQuery(id+"F6.boolean.opBoolean","SPLIT",EDGE,{"disambiguationData":[TD([makeQuery(id+"F6.opExtrude","SWEPT_FACE",FACE,{"disambiguationData":[OSD([sQuery(id+"F5.wireOp",EDGE,"E38.2.0.0")])]})])],"derivedFrom":makeQuery(id+"F2.opExtrude","SWEPT_EDGE",EDGE,{"disambiguationData":[OSD([subQ1,subQ0])]})});}
            var Q21;
            {var subQ0=sQuery(id+"F0.wireOp",EDGE,"E1.right");var subQ1=sQuery(id+"F0.wireOp",EDGE,"E1.top");Q21=makeQuery(id+"F6.boolean.opBoolean","SPLIT",EDGE,{"disambiguationData":[TD([makeQuery(id+"F6.opExtrude","SWEPT_FACE",FACE,{"disambiguationData":[OSD([sQuery(id+"F5.wireOp",EDGE,"E38.1.0.0")])]})])],"derivedFrom":makeQuery(id+"F2.opExtrude","SWEPT_EDGE",EDGE,{"disambiguationData":[OSD([subQ1,subQ0])]})});}
            var Q22;
            {var subQ0=sQuery(id+"F0.wireOp",EDGE,"E1.right");var subQ1=sQuery(id+"F0.wireOp",EDGE,"E1.top");Q22=makeQuery(id+"F6.boolean.opBoolean","SPLIT",EDGE,{"disambiguationData":[TD([makeQuery(id+"F6.opExtrude","SWEPT_FACE",FACE,{"disambiguationData":[OSD([sQuery(id+"F5.wireOp",EDGE,"E37.top")])]})])],"derivedFrom":makeQuery(id+"F2.opExtrude","SWEPT_EDGE",EDGE,{"disambiguationData":[OSD([subQ1,subQ0])]})});}
            var Q23;
            {var subQ0=sQuery(id+"F0.wireOp",EDGE,"E1.top");var subQ1=sQuery(id+"F0.wireOp",EDGE,"E1.right");Q23=makeQuery(id+"F6.boolean.opBoolean","SPLIT",EDGE,{"disambiguationData":[TD([makeQuery(id+"F6.opExtrude","SWEPT_FACE",FACE,{"disambiguationData":[OSD([sQuery(id+"F5.wireOp",EDGE,"E37.bottom")])]})])],"derivedFrom":makeQuery(id+"F2.opExtrude","SWEPT_EDGE",EDGE,{"disambiguationData":[OSD([subQ0,subQ1])]})});}
            var Q24;
            Q24=makeQuery(id+"F4.opExtrude","CAP_EDGE",EDGE,{"disambiguationData":[OSD([sQuery(id+"F3.wireOp",EDGE,"E36.right")])],"isStart":false});
            var Q25;
            Q25=makeQuery(id+"F4.opExtrude","CAP_EDGE",EDGE,{"disambiguationData":[OSD([sQuery(id+"F3.wireOp",EDGE,"E36.left")])],"isStart":false});
            fillet(context, id + "F19", {"entities" : qUnion([Q0, Q1, Q2, Q3, Q4, Q5, Q6, Q7, Q8, Q9, Q10, Q11, Q12, Q13, Q14, Q15, Q16, Q17, Q18, Q19, Q20, Q21, Q22, Q23, Q24, Q25]), "radius" : 1.9 * mm, "tangentPropagation" : true, "allowEdgeOverflow" : false});
        }
        {
            var Q0;
            Q0=makeQuery(id+"F1.opExtrude","SWEPT_EDGE",EDGE,{"disambiguationData":[OSD([sQuery(id+"F0.wireOp",EDGE,"E0.top"),sQuery(id+"F0.wireOp",EDGE,"E0.right")])]});
            var Q1;
            Q1=makeQuery(id+"F1.opExtrude","CAP_EDGE",EDGE,{"disambiguationData":[OSD([sQuery(id+"F0.wireOp",EDGE,"E0.top")])],"isStart":true});
            var Q2;
            Q2=makeQuery(id+"F1.opExtrude","SWEPT_EDGE",EDGE,{"disambiguationData":[OSD([sQuery(id+"F0.wireOp",EDGE,"E0.top"),sQuery(id+"F0.wireOp",EDGE,"E0.left")])]});
            var Q3;
            Q3=makeQuery(id+"F1.opExtrude","CAP_EDGE",EDGE,{"disambiguationData":[OSD([sQuery(id+"F0.wireOp",EDGE,"E0.left")])],"isStart":true});
            var Q4;
            Q4=makeQuery(id+"F1.opExtrude","CAP_EDGE",EDGE,{"disambiguationData":[OSD([sQuery(id+"F0.wireOp",EDGE,"E0.right")])],"isStart":true});
            fillet(context, id + "F20", {"entities" : qUnion([Q0, Q1, Q2, Q3, Q4]), "radius" : 0.5 * mm, "tangentPropagation" : true, "allowEdgeOverflow" : false});
        }
    });
